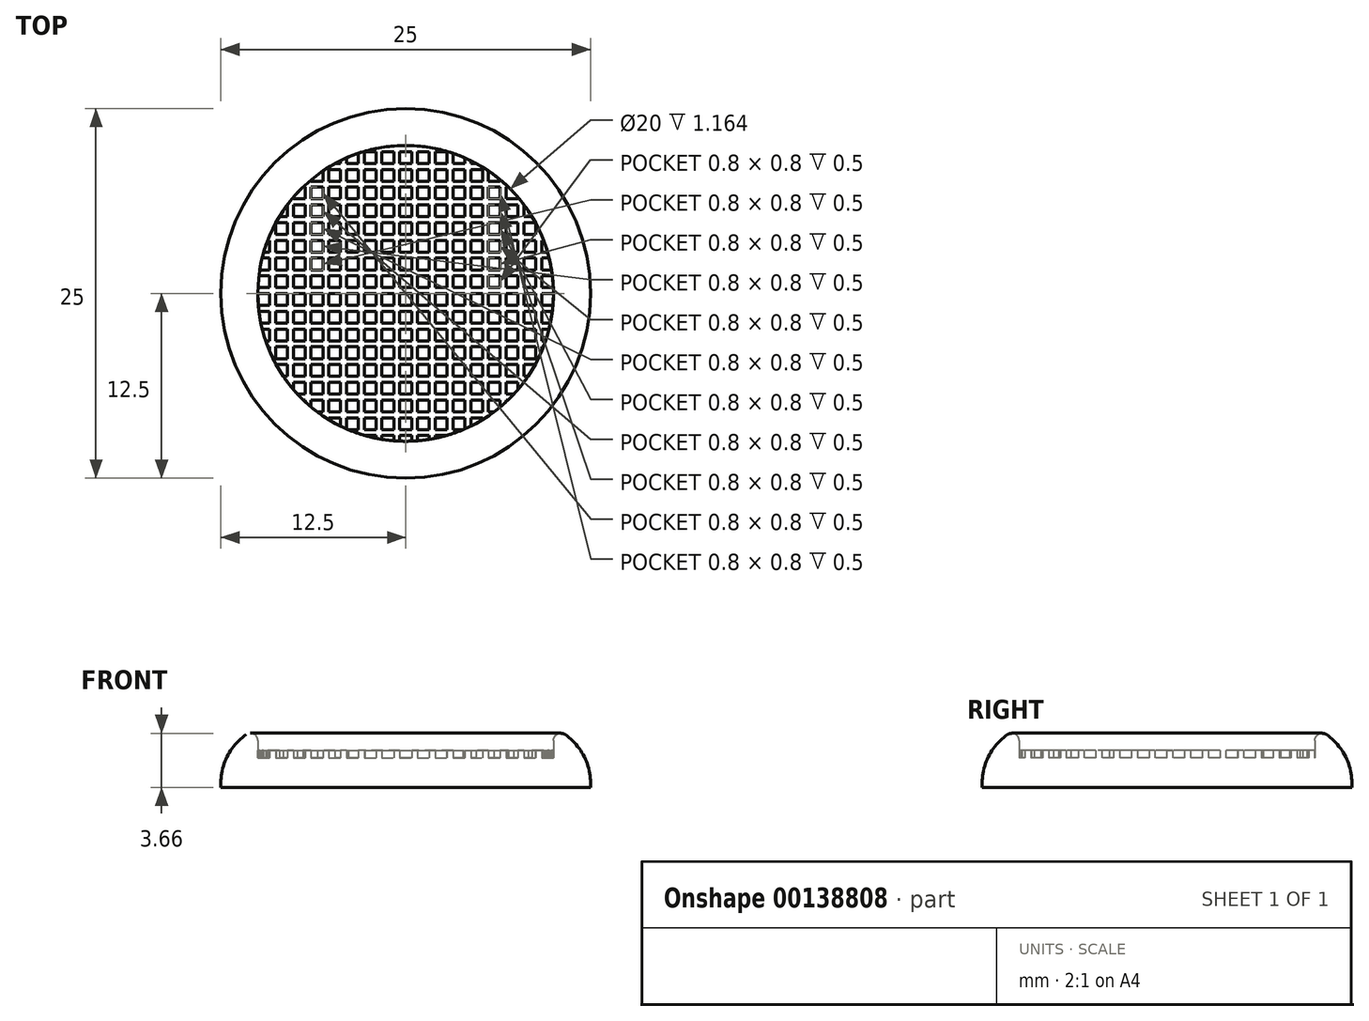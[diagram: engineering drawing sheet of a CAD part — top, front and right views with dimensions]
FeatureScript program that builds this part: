
annotation { "Feature Type Name" : "Feature", "Feature Type Description" : "" }
export const myFeature = defineFeature(function(context is Context, id is Id, definition is map)
    precondition{}
    {
        {
            var Q0;
            Q0=qCreatedBy(makeId("Top.planeOp"),FACE);
            var sketch = newSketch(context, id + "F0", { "sketchPlane" : qUnion([Q0])});
            skCircle(sketch, "E0", {"center": v(0, 0) * mm, "radius": 12.5 * mm});
            skCircle(sketch, "E1", {"center": v(0, 0) * mm, "radius": 10 * mm});
            skSolve(sketch);
        }
        {
            var Q0;
            Q0=makeQuery(id+"F0.imprint","IMPRINT",FACE,{"disambiguationData":[TD([[makeQuery(id+"F0.imprint","IMPRINT",EDGE,{"derivedFrom":sQuery(id+"F0.wireOp",EDGE,"E0")}),1.0]])]});
            var Q1;
            Q1=makeQuery(id+"F0.imprint","IMPRINT",FACE,{"disambiguationData":[TD([[makeQuery(id+"F0.imprint","IMPRINT",EDGE,{"derivedFrom":sQuery(id+"F0.wireOp",EDGE,"E1")}),1.0]])]});
            extrude(context, id + "F1", {"entities" : qUnion([Q0, Q1]), "depth" : 2 * mm});
        }
        {
            var Q0;
            Q0=makeQuery(id+"F0.imprint","IMPRINT",FACE,{"disambiguationData":[TD([[makeQuery(id+"F0.imprint","IMPRINT",EDGE,{"derivedFrom":sQuery(id+"F0.wireOp",EDGE,"E0")}),1.0]])]});
            extrude(context, id + "F2", {"entities" : qUnion([Q0]), "operationType" : NewBodyOperationType.ADD, "depth" : 4 * mm});
        }
        {
            var Q0;
            Q0=makeQuery(id+"F2.opExtrude","CAP_EDGE",EDGE,{"disambiguationData":[OSD([sQuery(id+"F0.wireOp",EDGE,"E0")])],"isStart":false});
            fillet(context, id + "F3", {"entities" : qUnion([Q0]), "radius" : 4 * mm, "tangentPropagation" : true, "allowEdgeOverflow" : false});
        }
        {
            var Q0;
            Q0=makeQuery(id+"F3.opFillet","BLEND_EDGE",EDGE,{"blendedFrom":[makeQuery(id+"F2.opExtrude","CAP_EDGE",EDGE,{"disambiguationData":[OSD([sQuery(id+"F0.wireOp",EDGE,"E0")])],"isStart":false}),makeQuery(id+"F2.opExtrude","SWEPT_FACE",FACE,{"disambiguationData":[OSD([sQuery(id+"F0.wireOp",EDGE,"E1")])]})],"blendedInto":[makeQuery(id+"F2.opExtrude","SWEPT_FACE",FACE,{"disambiguationData":[OSD([sQuery(id+"F0.wireOp",EDGE,"E1")])]})]});
            fillet(context, id + "F4", {"entities" : qUnion([Q0]), "radius" : 0.5 * mm, "tangentPropagation" : true, "allowEdgeOverflow" : false});
        }
        {
            var Q0;
            Q0=makeQuery(id+"F1.opExtrude","CAP_FACE",FACE,{"disambiguationData":[OSD([sQuery(id+"F0.wireOp",EDGE,"E0")])],"isStart":false});
            var sketch = newSketch(context, id + "F5", { "sketchPlane" : qUnion([Q0])});
            skLineSegment(sketch, "E2.bottom", {"start": v(-10, 10.79) * mm, "end": v(-9.2, 10.79) * mm});
            skLineSegment(sketch, "E2.top", {"start": v(-10, 9.99) * mm, "end": v(-9.2, 9.99) * mm});
            skLineSegment(sketch, "E2.left", {"start": v(-10, 10.79) * mm, "end": v(-10, 9.99) * mm});
            skLineSegment(sketch, "E2.right", {"start": v(-9.2, 10.79) * mm, "end": v(-9.2, 9.99) * mm});
            skCircle(sketch, "E3.0", {"center": v(0, 0) * mm, "radius": 10 * mm, "construction": true});
            skLineSegment(sketch, "E4", {"start": v(-10, 0) * mm, "end": v(-10, 10.79) * mm, "construction": true});
            skLineSegment(sketch, "E5", {"start": v(-10, 10.79) * mm, "end": v(0, 10.79) * mm, "construction": true});
            skLineSegment(sketch, "E6.1.0.0", {"start": v(-8.8, 10.79) * mm, "end": v(-8, 10.79) * mm});
            skLineSegment(sketch, "E6.1.0.1", {"start": v(-8.8, 9.99) * mm, "end": v(-8, 9.99) * mm});
            skLineSegment(sketch, "E6.1.0.2", {"start": v(-8, 10.79) * mm, "end": v(-8, 9.99) * mm});
            skLineSegment(sketch, "E6.1.0.3", {"start": v(-8.8, 10.79) * mm, "end": v(-8.8, 9.99) * mm});
            skLineSegment(sketch, "E6.2.0.0", {"start": v(-7.6, 10.79) * mm, "end": v(-6.8, 10.79) * mm});
            skLineSegment(sketch, "E6.2.0.1", {"start": v(-7.6, 9.99) * mm, "end": v(-6.8, 9.99) * mm});
            skLineSegment(sketch, "E6.2.0.2", {"start": v(-6.8, 10.79) * mm, "end": v(-6.8, 9.99) * mm});
            skLineSegment(sketch, "E6.2.0.3", {"start": v(-7.6, 10.79) * mm, "end": v(-7.6, 9.99) * mm});
            skLineSegment(sketch, "E6.3.0.0", {"start": v(-6.4, 10.79) * mm, "end": v(-5.6, 10.79) * mm});
            skLineSegment(sketch, "E6.3.0.1", {"start": v(-6.4, 9.99) * mm, "end": v(-5.6, 9.99) * mm});
            skLineSegment(sketch, "E6.3.0.2", {"start": v(-5.6, 10.79) * mm, "end": v(-5.6, 9.99) * mm});
            skLineSegment(sketch, "E6.3.0.3", {"start": v(-6.4, 10.79) * mm, "end": v(-6.4, 9.99) * mm});
            skLineSegment(sketch, "E6.4.0.0", {"start": v(-5.2, 10.79) * mm, "end": v(-4.4, 10.79) * mm});
            skLineSegment(sketch, "E6.4.0.1", {"start": v(-5.2, 9.99) * mm, "end": v(-4.4, 9.99) * mm});
            skLineSegment(sketch, "E6.4.0.2", {"start": v(-4.4, 10.79) * mm, "end": v(-4.4, 9.99) * mm});
            skLineSegment(sketch, "E6.4.0.3", {"start": v(-5.2, 10.79) * mm, "end": v(-5.2, 9.99) * mm});
            skLineSegment(sketch, "E6.5.0.0", {"start": v(-4, 10.79) * mm, "end": v(-3.2, 10.79) * mm});
            skLineSegment(sketch, "E6.5.0.1", {"start": v(-4, 9.99) * mm, "end": v(-3.2, 9.99) * mm});
            skLineSegment(sketch, "E6.5.0.2", {"start": v(-3.2, 10.79) * mm, "end": v(-3.2, 9.99) * mm});
            skLineSegment(sketch, "E6.5.0.3", {"start": v(-4, 10.79) * mm, "end": v(-4, 9.99) * mm});
            skLineSegment(sketch, "E6.6.0.0", {"start": v(-2.8, 10.79) * mm, "end": v(-2, 10.79) * mm});
            skLineSegment(sketch, "E6.6.0.1", {"start": v(-2.8, 9.99) * mm, "end": v(-2, 9.99) * mm});
            skLineSegment(sketch, "E6.6.0.2", {"start": v(-2, 10.79) * mm, "end": v(-2, 9.99) * mm});
            skLineSegment(sketch, "E6.6.0.3", {"start": v(-2.8, 10.79) * mm, "end": v(-2.8, 9.99) * mm});
            skLineSegment(sketch, "E6.7.0.0", {"start": v(-1.6, 10.79) * mm, "end": v(-0.8, 10.79) * mm});
            skLineSegment(sketch, "E6.7.0.1", {"start": v(-1.6, 9.99) * mm, "end": v(-0.8, 9.99) * mm});
            skLineSegment(sketch, "E6.7.0.2", {"start": v(-0.8, 10.79) * mm, "end": v(-0.8, 9.99) * mm});
            skLineSegment(sketch, "E6.7.0.3", {"start": v(-1.6, 10.79) * mm, "end": v(-1.6, 9.99) * mm});
            skLineSegment(sketch, "E6.8.0.0", {"start": v(-0.4, 10.79) * mm, "end": v(0.4, 10.79) * mm});
            skLineSegment(sketch, "E6.8.0.1", {"start": v(-0.4, 9.99) * mm, "end": v(0.4, 9.99) * mm});
            skLineSegment(sketch, "E6.8.0.2", {"start": v(0.4, 10.79) * mm, "end": v(0.4, 9.99) * mm});
            skLineSegment(sketch, "E6.8.0.3", {"start": v(-0.4, 10.79) * mm, "end": v(-0.4, 9.99) * mm});
            skLineSegment(sketch, "E6.9.0.0", {"start": v(0.8, 10.79) * mm, "end": v(1.6, 10.79) * mm});
            skLineSegment(sketch, "E6.9.0.1", {"start": v(0.8, 9.99) * mm, "end": v(1.6, 9.99) * mm});
            skLineSegment(sketch, "E6.9.0.2", {"start": v(1.6, 10.79) * mm, "end": v(1.6, 9.99) * mm});
            skLineSegment(sketch, "E6.9.0.3", {"start": v(0.8, 10.79) * mm, "end": v(0.8, 9.99) * mm});
            skLineSegment(sketch, "E6.10.0.0", {"start": v(2, 10.79) * mm, "end": v(2.8, 10.79) * mm});
            skLineSegment(sketch, "E6.10.0.1", {"start": v(2, 9.99) * mm, "end": v(2.8, 9.99) * mm});
            skLineSegment(sketch, "E6.10.0.2", {"start": v(2.8, 10.79) * mm, "end": v(2.8, 9.99) * mm});
            skLineSegment(sketch, "E6.10.0.3", {"start": v(2, 10.79) * mm, "end": v(2, 9.99) * mm});
            skLineSegment(sketch, "E6.11.0.0", {"start": v(3.2, 10.79) * mm, "end": v(4, 10.79) * mm});
            skLineSegment(sketch, "E6.11.0.1", {"start": v(3.2, 9.99) * mm, "end": v(4, 9.99) * mm});
            skLineSegment(sketch, "E6.11.0.2", {"start": v(4, 10.79) * mm, "end": v(4, 9.99) * mm});
            skLineSegment(sketch, "E6.11.0.3", {"start": v(3.2, 10.79) * mm, "end": v(3.2, 9.99) * mm});
            skLineSegment(sketch, "E6.12.0.0", {"start": v(4.4, 10.79) * mm, "end": v(5.2, 10.79) * mm});
            skLineSegment(sketch, "E6.12.0.1", {"start": v(4.4, 9.99) * mm, "end": v(5.2, 9.99) * mm});
            skLineSegment(sketch, "E6.12.0.2", {"start": v(5.2, 10.79) * mm, "end": v(5.2, 9.99) * mm});
            skLineSegment(sketch, "E6.12.0.3", {"start": v(4.4, 10.79) * mm, "end": v(4.4, 9.99) * mm});
            skLineSegment(sketch, "E6.13.0.0", {"start": v(5.6, 10.79) * mm, "end": v(6.4, 10.79) * mm});
            skLineSegment(sketch, "E6.13.0.1", {"start": v(5.6, 9.99) * mm, "end": v(6.4, 9.99) * mm});
            skLineSegment(sketch, "E6.13.0.2", {"start": v(6.4, 10.79) * mm, "end": v(6.4, 9.99) * mm});
            skLineSegment(sketch, "E6.13.0.3", {"start": v(5.6, 10.79) * mm, "end": v(5.6, 9.99) * mm});
            skLineSegment(sketch, "E6.14.0.0", {"start": v(6.8, 10.79) * mm, "end": v(7.6, 10.79) * mm});
            skLineSegment(sketch, "E6.14.0.1", {"start": v(6.8, 9.99) * mm, "end": v(7.6, 9.99) * mm});
            skLineSegment(sketch, "E6.14.0.2", {"start": v(7.6, 10.79) * mm, "end": v(7.6, 9.99) * mm});
            skLineSegment(sketch, "E6.14.0.3", {"start": v(6.8, 10.79) * mm, "end": v(6.8, 9.99) * mm});
            skLineSegment(sketch, "E6.15.0.0", {"start": v(8, 10.79) * mm, "end": v(8.8, 10.79) * mm});
            skLineSegment(sketch, "E6.15.0.1", {"start": v(8, 9.99) * mm, "end": v(8.8, 9.99) * mm});
            skLineSegment(sketch, "E6.15.0.2", {"start": v(8.8, 10.79) * mm, "end": v(8.8, 9.99) * mm});
            skLineSegment(sketch, "E6.15.0.3", {"start": v(8, 10.79) * mm, "end": v(8, 9.99) * mm});
            skLineSegment(sketch, "E6.16.0.0", {"start": v(9.2, 10.79) * mm, "end": v(10, 10.79) * mm});
            skLineSegment(sketch, "E6.16.0.1", {"start": v(9.2, 9.99) * mm, "end": v(10, 9.99) * mm});
            skLineSegment(sketch, "E6.16.0.2", {"start": v(10, 10.79) * mm, "end": v(10, 9.99) * mm});
            skLineSegment(sketch, "E6.16.0.3", {"start": v(9.2, 10.79) * mm, "end": v(9.2, 9.99) * mm});
            skLineSegment(sketch, "E6.direction1", {"start": v(-10, 9.99) * mm, "end": v(-8.8, 9.99) * mm, "construction": true});
            skLineSegment(sketch, "E7.1.0.0", {"start": v(6.8, 9.59) * mm, "end": v(6.8, 8.79) * mm});
            skLineSegment(sketch, "E7.1.0.1", {"start": v(6.8, 8.79) * mm, "end": v(7.6, 8.79) * mm});
            skLineSegment(sketch, "E7.1.0.2", {"start": v(6.8, 9.59) * mm, "end": v(7.6, 9.59) * mm});
            skLineSegment(sketch, "E7.1.0.3", {"start": v(6.4, 9.59) * mm, "end": v(6.4, 8.79) * mm});
            skLineSegment(sketch, "E7.1.0.4", {"start": v(5.6, 8.79) * mm, "end": v(6.4, 8.79) * mm});
            skLineSegment(sketch, "E7.1.0.5", {"start": v(5.6, 9.59) * mm, "end": v(6.4, 9.59) * mm});
            skLineSegment(sketch, "E7.1.0.6", {"start": v(10, 9.59) * mm, "end": v(10, 8.79) * mm});
            skLineSegment(sketch, "E7.1.0.7", {"start": v(9.2, 8.79) * mm, "end": v(10, 8.79) * mm});
            skLineSegment(sketch, "E7.1.0.8", {"start": v(9.2, 9.59) * mm, "end": v(10, 9.59) * mm});
            skLineSegment(sketch, "E7.1.0.9", {"start": v(2, 9.59) * mm, "end": v(2, 8.79) * mm});
            skLineSegment(sketch, "E7.1.0.10", {"start": v(-2.8, 9.59) * mm, "end": v(-2.8, 8.79) * mm});
            skLineSegment(sketch, "E7.1.0.11", {"start": v(-7.6, 8.79) * mm, "end": v(-6.8, 8.79) * mm});
            skLineSegment(sketch, "E7.1.0.12", {"start": v(-7.6, 9.59) * mm, "end": v(-6.8, 9.59) * mm});
            skLineSegment(sketch, "E7.1.0.13", {"start": v(-2.8, 8.79) * mm, "end": v(-2, 8.79) * mm});
            skLineSegment(sketch, "E7.1.0.14", {"start": v(2, 8.79) * mm, "end": v(2.8, 8.79) * mm});
            skLineSegment(sketch, "E7.1.0.15", {"start": v(-8.8, 9.59) * mm, "end": v(-8.8, 8.79) * mm});
            skLineSegment(sketch, "E7.1.0.16", {"start": v(-8, 9.59) * mm, "end": v(-8, 8.79) * mm});
            skLineSegment(sketch, "E7.1.0.17", {"start": v(-8.8, 8.79) * mm, "end": v(-8, 8.79) * mm});
            skLineSegment(sketch, "E7.1.0.18", {"start": v(-10, 9.59) * mm, "end": v(0, 9.59) * mm, "construction": true});
            skLineSegment(sketch, "E7.1.0.19", {"start": v(-9.2, 9.59) * mm, "end": v(-9.2, 8.79) * mm});
            skLineSegment(sketch, "E7.1.0.20", {"start": v(-6.4, 9.59) * mm, "end": v(-5.6, 9.59) * mm});
            skLineSegment(sketch, "E7.1.0.21", {"start": v(-7.6, 9.59) * mm, "end": v(-7.6, 8.79) * mm});
            skLineSegment(sketch, "E7.1.0.22", {"start": v(-6.8, 9.59) * mm, "end": v(-6.8, 8.79) * mm});
            skLineSegment(sketch, "E7.1.0.23", {"start": v(2.8, 9.59) * mm, "end": v(2.8, 8.79) * mm});
            skLineSegment(sketch, "E7.1.0.24", {"start": v(7.6, 9.59) * mm, "end": v(7.6, 8.79) * mm});
            skLineSegment(sketch, "E7.1.0.25", {"start": v(-2, 9.59) * mm, "end": v(-2, 8.79) * mm});
            skLineSegment(sketch, "E7.1.0.26", {"start": v(2, 9.59) * mm, "end": v(2.8, 9.59) * mm});
            skLineSegment(sketch, "E7.1.0.27", {"start": v(-4, 9.59) * mm, "end": v(-4, 8.79) * mm});
            skLineSegment(sketch, "E7.1.0.28", {"start": v(0.8, 9.59) * mm, "end": v(0.8, 8.79) * mm});
            skLineSegment(sketch, "E7.1.0.29", {"start": v(5.6, 9.59) * mm, "end": v(5.6, 8.79) * mm});
            skLineSegment(sketch, "E7.1.0.30", {"start": v(-3.2, 9.59) * mm, "end": v(-3.2, 8.79) * mm});
            skLineSegment(sketch, "E7.1.0.31", {"start": v(1.6, 9.59) * mm, "end": v(1.6, 8.79) * mm});
            skLineSegment(sketch, "E7.1.0.32", {"start": v(-4, 8.79) * mm, "end": v(-3.2, 8.79) * mm});
            skLineSegment(sketch, "E7.1.0.33", {"start": v(0.8, 8.79) * mm, "end": v(1.6, 8.79) * mm});
            skLineSegment(sketch, "E7.1.0.34", {"start": v(0.8, 9.59) * mm, "end": v(1.6, 9.59) * mm});
            skLineSegment(sketch, "E7.1.0.35", {"start": v(-10, 8.79) * mm, "end": v(-8.8, 8.79) * mm, "construction": true});
            skLineSegment(sketch, "E7.1.0.36", {"start": v(4.4, 9.59) * mm, "end": v(4.4, 8.79) * mm});
            skLineSegment(sketch, "E7.1.0.37", {"start": v(9.2, 9.59) * mm, "end": v(9.2, 8.79) * mm});
            skLineSegment(sketch, "E7.1.0.38", {"start": v(-5.2, 9.59) * mm, "end": v(-5.2, 8.79) * mm});
            skLineSegment(sketch, "E7.1.0.39", {"start": v(-0.4, 9.59) * mm, "end": v(-0.4, 8.79) * mm});
            skLineSegment(sketch, "E7.1.0.40", {"start": v(5.2, 9.59) * mm, "end": v(5.2, 8.79) * mm});
            skLineSegment(sketch, "E7.1.0.41", {"start": v(-4.4, 9.59) * mm, "end": v(-4.4, 8.79) * mm});
            skLineSegment(sketch, "E7.1.0.42", {"start": v(0.4, 9.59) * mm, "end": v(0.4, 8.79) * mm});
            skLineSegment(sketch, "E7.1.0.43", {"start": v(4.4, 8.79) * mm, "end": v(5.2, 8.79) * mm});
            skLineSegment(sketch, "E7.1.0.44", {"start": v(-5.2, 8.79) * mm, "end": v(-4.4, 8.79) * mm});
            skLineSegment(sketch, "E7.1.0.45", {"start": v(-0.4, 8.79) * mm, "end": v(0.4, 8.79) * mm});
            skLineSegment(sketch, "E7.1.0.46", {"start": v(4.4, 9.59) * mm, "end": v(5.2, 9.59) * mm});
            skLineSegment(sketch, "E7.1.0.47", {"start": v(-0.4, 9.59) * mm, "end": v(0.4, 9.59) * mm});
            skLineSegment(sketch, "E7.1.0.48", {"start": v(3.2, 9.59) * mm, "end": v(3.2, 8.79) * mm});
            skLineSegment(sketch, "E7.1.0.49", {"start": v(8, 9.59) * mm, "end": v(8, 8.79) * mm});
            skLineSegment(sketch, "E7.1.0.50", {"start": v(-6.4, 9.59) * mm, "end": v(-6.4, 8.79) * mm});
            skLineSegment(sketch, "E7.1.0.51", {"start": v(-1.6, 9.59) * mm, "end": v(-1.6, 8.79) * mm});
            skLineSegment(sketch, "E7.1.0.52", {"start": v(-5.6, 9.59) * mm, "end": v(-5.6, 8.79) * mm});
            skLineSegment(sketch, "E7.1.0.53", {"start": v(-0.8, 9.59) * mm, "end": v(-0.8, 8.79) * mm});
            skLineSegment(sketch, "E7.1.0.54", {"start": v(4, 9.59) * mm, "end": v(4, 8.79) * mm});
            skLineSegment(sketch, "E7.1.0.55", {"start": v(8.8, 9.59) * mm, "end": v(8.8, 8.79) * mm});
            skLineSegment(sketch, "E7.1.0.56", {"start": v(3.2, 8.79) * mm, "end": v(4, 8.79) * mm});
            skLineSegment(sketch, "E7.1.0.57", {"start": v(8, 8.79) * mm, "end": v(8.8, 8.79) * mm});
            skLineSegment(sketch, "E7.1.0.58", {"start": v(-6.4, 8.79) * mm, "end": v(-5.6, 8.79) * mm});
            skLineSegment(sketch, "E7.1.0.59", {"start": v(-1.6, 8.79) * mm, "end": v(-0.8, 8.79) * mm});
            skLineSegment(sketch, "E7.1.0.60", {"start": v(3.2, 9.59) * mm, "end": v(4, 9.59) * mm});
            skLineSegment(sketch, "E7.1.0.61", {"start": v(8, 9.59) * mm, "end": v(8.8, 9.59) * mm});
            skLineSegment(sketch, "E7.1.0.62", {"start": v(-8.8, 9.59) * mm, "end": v(-8, 9.59) * mm});
            skLineSegment(sketch, "E7.1.0.63", {"start": v(-10, 9.59) * mm, "end": v(-10, 8.79) * mm});
            skLineSegment(sketch, "E7.1.0.64", {"start": v(-10, 8.79) * mm, "end": v(-9.2, 8.79) * mm});
            skLineSegment(sketch, "E7.1.0.65", {"start": v(-10, 9.59) * mm, "end": v(-9.2, 9.59) * mm});
            skLineSegment(sketch, "E7.1.0.66", {"start": v(-2.8, 9.59) * mm, "end": v(-2, 9.59) * mm});
            skLineSegment(sketch, "E7.1.0.67", {"start": v(-4, 9.59) * mm, "end": v(-3.2, 9.59) * mm});
            skLineSegment(sketch, "E7.1.0.68", {"start": v(-5.2, 9.59) * mm, "end": v(-4.4, 9.59) * mm});
            skLineSegment(sketch, "E7.1.0.69", {"start": v(-1.6, 9.59) * mm, "end": v(-0.8, 9.59) * mm});
            skLineSegment(sketch, "E7.2.0.0", {"start": v(6.8, 8.39) * mm, "end": v(6.8, 7.59) * mm});
            skLineSegment(sketch, "E7.2.0.1", {"start": v(6.8, 7.59) * mm, "end": v(7.6, 7.59) * mm});
            skLineSegment(sketch, "E7.2.0.2", {"start": v(6.8, 8.39) * mm, "end": v(7.6, 8.39) * mm});
            skLineSegment(sketch, "E7.2.0.3", {"start": v(6.4, 8.39) * mm, "end": v(6.4, 7.59) * mm});
            skLineSegment(sketch, "E7.2.0.4", {"start": v(5.6, 7.59) * mm, "end": v(6.4, 7.59) * mm});
            skLineSegment(sketch, "E7.2.0.5", {"start": v(5.6, 8.39) * mm, "end": v(6.4, 8.39) * mm});
            skLineSegment(sketch, "E7.2.0.6", {"start": v(10, 8.39) * mm, "end": v(10, 7.59) * mm});
            skLineSegment(sketch, "E7.2.0.7", {"start": v(9.2, 7.59) * mm, "end": v(10, 7.59) * mm});
            skLineSegment(sketch, "E7.2.0.8", {"start": v(9.2, 8.39) * mm, "end": v(10, 8.39) * mm});
            skLineSegment(sketch, "E7.2.0.9", {"start": v(2, 8.39) * mm, "end": v(2, 7.59) * mm});
            skLineSegment(sketch, "E7.2.0.10", {"start": v(-2.8, 8.39) * mm, "end": v(-2.8, 7.59) * mm});
            skLineSegment(sketch, "E7.2.0.11", {"start": v(-7.6, 7.59) * mm, "end": v(-6.8, 7.59) * mm});
            skLineSegment(sketch, "E7.2.0.12", {"start": v(-7.6, 8.39) * mm, "end": v(-6.8, 8.39) * mm});
            skLineSegment(sketch, "E7.2.0.13", {"start": v(-2.8, 7.59) * mm, "end": v(-2, 7.59) * mm});
            skLineSegment(sketch, "E7.2.0.14", {"start": v(2, 7.59) * mm, "end": v(2.8, 7.59) * mm});
            skLineSegment(sketch, "E7.2.0.15", {"start": v(-8.8, 8.39) * mm, "end": v(-8.8, 7.59) * mm});
            skLineSegment(sketch, "E7.2.0.16", {"start": v(-8, 8.39) * mm, "end": v(-8, 7.59) * mm});
            skLineSegment(sketch, "E7.2.0.17", {"start": v(-8.8, 7.59) * mm, "end": v(-8, 7.59) * mm});
            skLineSegment(sketch, "E7.2.0.18", {"start": v(-10, 8.39) * mm, "end": v(0, 8.39) * mm, "construction": true});
            skLineSegment(sketch, "E7.2.0.19", {"start": v(-9.2, 8.39) * mm, "end": v(-9.2, 7.59) * mm});
            skLineSegment(sketch, "E7.2.0.20", {"start": v(-6.4, 8.39) * mm, "end": v(-5.6, 8.39) * mm});
            skLineSegment(sketch, "E7.2.0.21", {"start": v(-7.6, 8.39) * mm, "end": v(-7.6, 7.59) * mm});
            skLineSegment(sketch, "E7.2.0.22", {"start": v(-6.8, 8.39) * mm, "end": v(-6.8, 7.59) * mm});
            skLineSegment(sketch, "E7.2.0.23", {"start": v(2.8, 8.39) * mm, "end": v(2.8, 7.59) * mm});
            skLineSegment(sketch, "E7.2.0.24", {"start": v(7.6, 8.39) * mm, "end": v(7.6, 7.59) * mm});
            skLineSegment(sketch, "E7.2.0.25", {"start": v(-2, 8.39) * mm, "end": v(-2, 7.59) * mm});
            skLineSegment(sketch, "E7.2.0.26", {"start": v(2, 8.39) * mm, "end": v(2.8, 8.39) * mm});
            skLineSegment(sketch, "E7.2.0.27", {"start": v(-4, 8.39) * mm, "end": v(-4, 7.59) * mm});
            skLineSegment(sketch, "E7.2.0.28", {"start": v(0.8, 8.39) * mm, "end": v(0.8, 7.59) * mm});
            skLineSegment(sketch, "E7.2.0.29", {"start": v(5.6, 8.39) * mm, "end": v(5.6, 7.59) * mm});
            skLineSegment(sketch, "E7.2.0.30", {"start": v(-3.2, 8.39) * mm, "end": v(-3.2, 7.59) * mm});
            skLineSegment(sketch, "E7.2.0.31", {"start": v(1.6, 8.39) * mm, "end": v(1.6, 7.59) * mm});
            skLineSegment(sketch, "E7.2.0.32", {"start": v(-4, 7.59) * mm, "end": v(-3.2, 7.59) * mm});
            skLineSegment(sketch, "E7.2.0.33", {"start": v(0.8, 7.59) * mm, "end": v(1.6, 7.59) * mm});
            skLineSegment(sketch, "E7.2.0.34", {"start": v(0.8, 8.39) * mm, "end": v(1.6, 8.39) * mm});
            skLineSegment(sketch, "E7.2.0.35", {"start": v(-10, 7.59) * mm, "end": v(-8.8, 7.59) * mm, "construction": true});
            skLineSegment(sketch, "E7.2.0.36", {"start": v(4.4, 8.39) * mm, "end": v(4.4, 7.59) * mm});
            skLineSegment(sketch, "E7.2.0.37", {"start": v(9.2, 8.39) * mm, "end": v(9.2, 7.59) * mm});
            skLineSegment(sketch, "E7.2.0.38", {"start": v(-5.2, 8.39) * mm, "end": v(-5.2, 7.59) * mm});
            skLineSegment(sketch, "E7.2.0.39", {"start": v(-0.4, 8.39) * mm, "end": v(-0.4, 7.59) * mm});
            skLineSegment(sketch, "E7.2.0.40", {"start": v(5.2, 8.39) * mm, "end": v(5.2, 7.59) * mm});
            skLineSegment(sketch, "E7.2.0.41", {"start": v(-4.4, 8.39) * mm, "end": v(-4.4, 7.59) * mm});
            skLineSegment(sketch, "E7.2.0.42", {"start": v(0.4, 8.39) * mm, "end": v(0.4, 7.59) * mm});
            skLineSegment(sketch, "E7.2.0.43", {"start": v(4.4, 7.59) * mm, "end": v(5.2, 7.59) * mm});
            skLineSegment(sketch, "E7.2.0.44", {"start": v(-5.2, 7.59) * mm, "end": v(-4.4, 7.59) * mm});
            skLineSegment(sketch, "E7.2.0.45", {"start": v(-0.4, 7.59) * mm, "end": v(0.4, 7.59) * mm});
            skLineSegment(sketch, "E7.2.0.46", {"start": v(4.4, 8.39) * mm, "end": v(5.2, 8.39) * mm});
            skLineSegment(sketch, "E7.2.0.47", {"start": v(-0.4, 8.39) * mm, "end": v(0.4, 8.39) * mm});
            skLineSegment(sketch, "E7.2.0.48", {"start": v(3.2, 8.39) * mm, "end": v(3.2, 7.59) * mm});
            skLineSegment(sketch, "E7.2.0.49", {"start": v(8, 8.39) * mm, "end": v(8, 7.59) * mm});
            skLineSegment(sketch, "E7.2.0.50", {"start": v(-6.4, 8.39) * mm, "end": v(-6.4, 7.59) * mm});
            skLineSegment(sketch, "E7.2.0.51", {"start": v(-1.6, 8.39) * mm, "end": v(-1.6, 7.59) * mm});
            skLineSegment(sketch, "E7.2.0.52", {"start": v(-5.6, 8.39) * mm, "end": v(-5.6, 7.59) * mm});
            skLineSegment(sketch, "E7.2.0.53", {"start": v(-0.8, 8.39) * mm, "end": v(-0.8, 7.59) * mm});
            skLineSegment(sketch, "E7.2.0.54", {"start": v(4, 8.39) * mm, "end": v(4, 7.59) * mm});
            skLineSegment(sketch, "E7.2.0.55", {"start": v(8.8, 8.39) * mm, "end": v(8.8, 7.59) * mm});
            skLineSegment(sketch, "E7.2.0.56", {"start": v(3.2, 7.59) * mm, "end": v(4, 7.59) * mm});
            skLineSegment(sketch, "E7.2.0.57", {"start": v(8, 7.59) * mm, "end": v(8.8, 7.59) * mm});
            skLineSegment(sketch, "E7.2.0.58", {"start": v(-6.4, 7.59) * mm, "end": v(-5.6, 7.59) * mm});
            skLineSegment(sketch, "E7.2.0.59", {"start": v(-1.6, 7.59) * mm, "end": v(-0.8, 7.59) * mm});
            skLineSegment(sketch, "E7.2.0.60", {"start": v(3.2, 8.39) * mm, "end": v(4, 8.39) * mm});
            skLineSegment(sketch, "E7.2.0.61", {"start": v(8, 8.39) * mm, "end": v(8.8, 8.39) * mm});
            skLineSegment(sketch, "E7.2.0.62", {"start": v(-8.8, 8.39) * mm, "end": v(-8, 8.39) * mm});
            skLineSegment(sketch, "E7.2.0.63", {"start": v(-10, 8.39) * mm, "end": v(-10, 7.59) * mm});
            skLineSegment(sketch, "E7.2.0.64", {"start": v(-10, 7.59) * mm, "end": v(-9.2, 7.59) * mm});
            skLineSegment(sketch, "E7.2.0.65", {"start": v(-10, 8.39) * mm, "end": v(-9.2, 8.39) * mm});
            skLineSegment(sketch, "E7.2.0.66", {"start": v(-2.8, 8.39) * mm, "end": v(-2, 8.39) * mm});
            skLineSegment(sketch, "E7.2.0.67", {"start": v(-4, 8.39) * mm, "end": v(-3.2, 8.39) * mm});
            skLineSegment(sketch, "E7.2.0.68", {"start": v(-5.2, 8.39) * mm, "end": v(-4.4, 8.39) * mm});
            skLineSegment(sketch, "E7.2.0.69", {"start": v(-1.6, 8.39) * mm, "end": v(-0.8, 8.39) * mm});
            skLineSegment(sketch, "E7.direction1", {"start": v(-10, 9.99) * mm, "end": v(-10, 8.79) * mm, "construction": true});
            skLineSegment(sketch, "E8.0.3.0", {"start": v(6.8, 7.19) * mm, "end": v(6.8, 6.39) * mm});
            skLineSegment(sketch, "E8.3.3.0", {"start": v(6.8, 6.39) * mm, "end": v(7.6, 6.39) * mm});
            skLineSegment(sketch, "E8.6.3.0", {"start": v(6.8, 7.19) * mm, "end": v(7.6, 7.19) * mm});
            skLineSegment(sketch, "E8.9.3.0", {"start": v(6.4, 7.19) * mm, "end": v(6.4, 6.39) * mm});
            skLineSegment(sketch, "E8.12.3.0", {"start": v(5.6, 6.39) * mm, "end": v(6.4, 6.39) * mm});
            skLineSegment(sketch, "E8.15.3.0", {"start": v(5.6, 7.19) * mm, "end": v(6.4, 7.19) * mm});
            skLineSegment(sketch, "E8.18.3.0", {"start": v(10, 7.19) * mm, "end": v(10, 6.39) * mm});
            skLineSegment(sketch, "E8.21.3.0", {"start": v(9.2, 6.39) * mm, "end": v(10, 6.39) * mm});
            skLineSegment(sketch, "E8.24.3.0", {"start": v(9.2, 7.19) * mm, "end": v(10, 7.19) * mm});
            skLineSegment(sketch, "E8.27.3.0", {"start": v(2, 7.19) * mm, "end": v(2, 6.39) * mm});
            skLineSegment(sketch, "E8.30.3.0", {"start": v(-2.8, 7.19) * mm, "end": v(-2.8, 6.39) * mm});
            skLineSegment(sketch, "E8.33.3.0", {"start": v(-7.6, 6.39) * mm, "end": v(-6.8, 6.39) * mm});
            skLineSegment(sketch, "E8.36.3.0", {"start": v(-7.6, 7.19) * mm, "end": v(-6.8, 7.19) * mm});
            skLineSegment(sketch, "E8.39.3.0", {"start": v(-2.8, 6.39) * mm, "end": v(-2, 6.39) * mm});
            skLineSegment(sketch, "E8.42.3.0", {"start": v(2, 6.39) * mm, "end": v(2.8, 6.39) * mm});
            skLineSegment(sketch, "E8.45.3.0", {"start": v(-8.8, 7.19) * mm, "end": v(-8.8, 6.39) * mm});
            skLineSegment(sketch, "E8.48.3.0", {"start": v(-8, 7.19) * mm, "end": v(-8, 6.39) * mm});
            skLineSegment(sketch, "E8.51.3.0", {"start": v(-8.8, 6.39) * mm, "end": v(-8, 6.39) * mm});
            skLineSegment(sketch, "E8.54.3.0", {"start": v(-10, 7.19) * mm, "end": v(0, 7.19) * mm, "construction": true});
            skLineSegment(sketch, "E8.57.3.0", {"start": v(-9.2, 7.19) * mm, "end": v(-9.2, 6.39) * mm});
            skLineSegment(sketch, "E8.60.3.0", {"start": v(-6.4, 7.19) * mm, "end": v(-5.6, 7.19) * mm});
            skLineSegment(sketch, "E8.63.3.0", {"start": v(-7.6, 7.19) * mm, "end": v(-7.6, 6.39) * mm});
            skLineSegment(sketch, "E8.66.3.0", {"start": v(-6.8, 7.19) * mm, "end": v(-6.8, 6.39) * mm});
            skLineSegment(sketch, "E8.69.3.0", {"start": v(2.8, 7.19) * mm, "end": v(2.8, 6.39) * mm});
            skLineSegment(sketch, "E8.72.3.0", {"start": v(7.6, 7.19) * mm, "end": v(7.6, 6.39) * mm});
            skLineSegment(sketch, "E8.75.3.0", {"start": v(-2, 7.19) * mm, "end": v(-2, 6.39) * mm});
            skLineSegment(sketch, "E8.78.3.0", {"start": v(2, 7.19) * mm, "end": v(2.8, 7.19) * mm});
            skLineSegment(sketch, "E8.81.3.0", {"start": v(-4, 7.19) * mm, "end": v(-4, 6.39) * mm});
            skLineSegment(sketch, "E8.84.3.0", {"start": v(0.8, 7.19) * mm, "end": v(0.8, 6.39) * mm});
            skLineSegment(sketch, "E8.87.3.0", {"start": v(5.6, 7.19) * mm, "end": v(5.6, 6.39) * mm});
            skLineSegment(sketch, "E8.90.3.0", {"start": v(-3.2, 7.19) * mm, "end": v(-3.2, 6.39) * mm});
            skLineSegment(sketch, "E8.93.3.0", {"start": v(1.6, 7.19) * mm, "end": v(1.6, 6.39) * mm});
            skLineSegment(sketch, "E8.96.3.0", {"start": v(-4, 6.39) * mm, "end": v(-3.2, 6.39) * mm});
            skLineSegment(sketch, "E8.99.3.0", {"start": v(0.8, 6.39) * mm, "end": v(1.6, 6.39) * mm});
            skLineSegment(sketch, "E8.102.3.0", {"start": v(0.8, 7.19) * mm, "end": v(1.6, 7.19) * mm});
            skLineSegment(sketch, "E8.105.3.0", {"start": v(-10, 6.39) * mm, "end": v(-8.8, 6.39) * mm, "construction": true});
            skLineSegment(sketch, "E8.108.3.0", {"start": v(4.4, 7.19) * mm, "end": v(4.4, 6.39) * mm});
            skLineSegment(sketch, "E8.111.3.0", {"start": v(9.2, 7.19) * mm, "end": v(9.2, 6.39) * mm});
            skLineSegment(sketch, "E8.114.3.0", {"start": v(-5.2, 7.19) * mm, "end": v(-5.2, 6.39) * mm});
            skLineSegment(sketch, "E8.117.3.0", {"start": v(-0.4, 7.19) * mm, "end": v(-0.4, 6.39) * mm});
            skLineSegment(sketch, "E8.120.3.0", {"start": v(5.2, 7.19) * mm, "end": v(5.2, 6.39) * mm});
            skLineSegment(sketch, "E8.123.3.0", {"start": v(-4.4, 7.19) * mm, "end": v(-4.4, 6.39) * mm});
            skLineSegment(sketch, "E8.126.3.0", {"start": v(0.4, 7.19) * mm, "end": v(0.4, 6.39) * mm});
            skLineSegment(sketch, "E8.129.3.0", {"start": v(4.4, 6.39) * mm, "end": v(5.2, 6.39) * mm});
            skLineSegment(sketch, "E8.132.3.0", {"start": v(-5.2, 6.39) * mm, "end": v(-4.4, 6.39) * mm});
            skLineSegment(sketch, "E8.135.3.0", {"start": v(-0.4, 6.39) * mm, "end": v(0.4, 6.39) * mm});
            skLineSegment(sketch, "E8.138.3.0", {"start": v(4.4, 7.19) * mm, "end": v(5.2, 7.19) * mm});
            skLineSegment(sketch, "E8.141.3.0", {"start": v(-0.4, 7.19) * mm, "end": v(0.4, 7.19) * mm});
            skLineSegment(sketch, "E8.144.3.0", {"start": v(3.2, 7.19) * mm, "end": v(3.2, 6.39) * mm});
            skLineSegment(sketch, "E8.147.3.0", {"start": v(8, 7.19) * mm, "end": v(8, 6.39) * mm});
            skLineSegment(sketch, "E8.150.3.0", {"start": v(-6.4, 7.19) * mm, "end": v(-6.4, 6.39) * mm});
            skLineSegment(sketch, "E8.153.3.0", {"start": v(-1.6, 7.19) * mm, "end": v(-1.6, 6.39) * mm});
            skLineSegment(sketch, "E8.156.3.0", {"start": v(-5.6, 7.19) * mm, "end": v(-5.6, 6.39) * mm});
            skLineSegment(sketch, "E8.159.3.0", {"start": v(-0.8, 7.19) * mm, "end": v(-0.8, 6.39) * mm});
            skLineSegment(sketch, "E8.162.3.0", {"start": v(4, 7.19) * mm, "end": v(4, 6.39) * mm});
            skLineSegment(sketch, "E8.165.3.0", {"start": v(8.8, 7.19) * mm, "end": v(8.8, 6.39) * mm});
            skLineSegment(sketch, "E8.168.3.0", {"start": v(3.2, 6.39) * mm, "end": v(4, 6.39) * mm});
            skLineSegment(sketch, "E8.171.3.0", {"start": v(8, 6.39) * mm, "end": v(8.8, 6.39) * mm});
            skLineSegment(sketch, "E8.174.3.0", {"start": v(-6.4, 6.39) * mm, "end": v(-5.6, 6.39) * mm});
            skLineSegment(sketch, "E8.177.3.0", {"start": v(-1.6, 6.39) * mm, "end": v(-0.8, 6.39) * mm});
            skLineSegment(sketch, "E8.180.3.0", {"start": v(3.2, 7.19) * mm, "end": v(4, 7.19) * mm});
            skLineSegment(sketch, "E8.183.3.0", {"start": v(8, 7.19) * mm, "end": v(8.8, 7.19) * mm});
            skLineSegment(sketch, "E8.186.3.0", {"start": v(-8.8, 7.19) * mm, "end": v(-8, 7.19) * mm});
            skLineSegment(sketch, "E8.189.3.0", {"start": v(-10, 7.19) * mm, "end": v(-10, 6.39) * mm});
            skLineSegment(sketch, "E8.192.3.0", {"start": v(-10, 6.39) * mm, "end": v(-9.2, 6.39) * mm});
            skLineSegment(sketch, "E8.195.3.0", {"start": v(-10, 7.19) * mm, "end": v(-9.2, 7.19) * mm});
            skLineSegment(sketch, "E8.198.3.0", {"start": v(-2.8, 7.19) * mm, "end": v(-2, 7.19) * mm});
            skLineSegment(sketch, "E8.201.3.0", {"start": v(-4, 7.19) * mm, "end": v(-3.2, 7.19) * mm});
            skLineSegment(sketch, "E8.204.3.0", {"start": v(-5.2, 7.19) * mm, "end": v(-4.4, 7.19) * mm});
            skLineSegment(sketch, "E8.207.3.0", {"start": v(-1.6, 7.19) * mm, "end": v(-0.8, 7.19) * mm});
            skLineSegment(sketch, "E8.0.4.0", {"start": v(6.8, 5.99) * mm, "end": v(6.8, 5.19) * mm});
            skLineSegment(sketch, "E8.3.4.0", {"start": v(6.8, 5.19) * mm, "end": v(7.6, 5.19) * mm});
            skLineSegment(sketch, "E8.6.4.0", {"start": v(6.8, 5.99) * mm, "end": v(7.6, 5.99) * mm});
            skLineSegment(sketch, "E8.9.4.0", {"start": v(6.4, 5.99) * mm, "end": v(6.4, 5.19) * mm});
            skLineSegment(sketch, "E8.12.4.0", {"start": v(5.6, 5.19) * mm, "end": v(6.4, 5.19) * mm});
            skLineSegment(sketch, "E8.15.4.0", {"start": v(5.6, 5.99) * mm, "end": v(6.4, 5.99) * mm});
            skLineSegment(sketch, "E8.18.4.0", {"start": v(10, 5.99) * mm, "end": v(10, 5.19) * mm});
            skLineSegment(sketch, "E8.21.4.0", {"start": v(9.2, 5.19) * mm, "end": v(10, 5.19) * mm});
            skLineSegment(sketch, "E8.24.4.0", {"start": v(9.2, 5.99) * mm, "end": v(10, 5.99) * mm});
            skLineSegment(sketch, "E8.27.4.0", {"start": v(2, 5.99) * mm, "end": v(2, 5.19) * mm});
            skLineSegment(sketch, "E8.30.4.0", {"start": v(-2.8, 5.99) * mm, "end": v(-2.8, 5.19) * mm});
            skLineSegment(sketch, "E8.33.4.0", {"start": v(-7.6, 5.19) * mm, "end": v(-6.8, 5.19) * mm});
            skLineSegment(sketch, "E8.36.4.0", {"start": v(-7.6, 5.99) * mm, "end": v(-6.8, 5.99) * mm});
            skLineSegment(sketch, "E8.39.4.0", {"start": v(-2.8, 5.19) * mm, "end": v(-2, 5.19) * mm});
            skLineSegment(sketch, "E8.42.4.0", {"start": v(2, 5.19) * mm, "end": v(2.8, 5.19) * mm});
            skLineSegment(sketch, "E8.45.4.0", {"start": v(-8.8, 5.99) * mm, "end": v(-8.8, 5.19) * mm});
            skLineSegment(sketch, "E8.48.4.0", {"start": v(-8, 5.99) * mm, "end": v(-8, 5.19) * mm});
            skLineSegment(sketch, "E8.51.4.0", {"start": v(-8.8, 5.19) * mm, "end": v(-8, 5.19) * mm});
            skLineSegment(sketch, "E8.54.4.0", {"start": v(-10, 5.99) * mm, "end": v(0, 5.99) * mm, "construction": true});
            skLineSegment(sketch, "E8.57.4.0", {"start": v(-9.2, 5.99) * mm, "end": v(-9.2, 5.19) * mm});
            skLineSegment(sketch, "E8.60.4.0", {"start": v(-6.4, 5.99) * mm, "end": v(-5.6, 5.99) * mm});
            skLineSegment(sketch, "E8.63.4.0", {"start": v(-7.6, 5.99) * mm, "end": v(-7.6, 5.19) * mm});
            skLineSegment(sketch, "E8.66.4.0", {"start": v(-6.8, 5.99) * mm, "end": v(-6.8, 5.19) * mm});
            skLineSegment(sketch, "E8.69.4.0", {"start": v(2.8, 5.99) * mm, "end": v(2.8, 5.19) * mm});
            skLineSegment(sketch, "E8.72.4.0", {"start": v(7.6, 5.99) * mm, "end": v(7.6, 5.19) * mm});
            skLineSegment(sketch, "E8.75.4.0", {"start": v(-2, 5.99) * mm, "end": v(-2, 5.19) * mm});
            skLineSegment(sketch, "E8.78.4.0", {"start": v(2, 5.99) * mm, "end": v(2.8, 5.99) * mm});
            skLineSegment(sketch, "E8.81.4.0", {"start": v(-4, 5.99) * mm, "end": v(-4, 5.19) * mm});
            skLineSegment(sketch, "E8.84.4.0", {"start": v(0.8, 5.99) * mm, "end": v(0.8, 5.19) * mm});
            skLineSegment(sketch, "E8.87.4.0", {"start": v(5.6, 5.99) * mm, "end": v(5.6, 5.19) * mm});
            skLineSegment(sketch, "E8.90.4.0", {"start": v(-3.2, 5.99) * mm, "end": v(-3.2, 5.19) * mm});
            skLineSegment(sketch, "E8.93.4.0", {"start": v(1.6, 5.99) * mm, "end": v(1.6, 5.19) * mm});
            skLineSegment(sketch, "E8.96.4.0", {"start": v(-4, 5.19) * mm, "end": v(-3.2, 5.19) * mm});
            skLineSegment(sketch, "E8.99.4.0", {"start": v(0.8, 5.19) * mm, "end": v(1.6, 5.19) * mm});
            skLineSegment(sketch, "E8.102.4.0", {"start": v(0.8, 5.99) * mm, "end": v(1.6, 5.99) * mm});
            skLineSegment(sketch, "E8.105.4.0", {"start": v(-10, 5.19) * mm, "end": v(-8.8, 5.19) * mm, "construction": true});
            skLineSegment(sketch, "E8.108.4.0", {"start": v(4.4, 5.99) * mm, "end": v(4.4, 5.19) * mm});
            skLineSegment(sketch, "E8.111.4.0", {"start": v(9.2, 5.99) * mm, "end": v(9.2, 5.19) * mm});
            skLineSegment(sketch, "E8.114.4.0", {"start": v(-5.2, 5.99) * mm, "end": v(-5.2, 5.19) * mm});
            skLineSegment(sketch, "E8.117.4.0", {"start": v(-0.4, 5.99) * mm, "end": v(-0.4, 5.19) * mm});
            skLineSegment(sketch, "E8.120.4.0", {"start": v(5.2, 5.99) * mm, "end": v(5.2, 5.19) * mm});
            skLineSegment(sketch, "E8.123.4.0", {"start": v(-4.4, 5.99) * mm, "end": v(-4.4, 5.19) * mm});
            skLineSegment(sketch, "E8.126.4.0", {"start": v(0.4, 5.99) * mm, "end": v(0.4, 5.19) * mm});
            skLineSegment(sketch, "E8.129.4.0", {"start": v(4.4, 5.19) * mm, "end": v(5.2, 5.19) * mm});
            skLineSegment(sketch, "E8.132.4.0", {"start": v(-5.2, 5.19) * mm, "end": v(-4.4, 5.19) * mm});
            skLineSegment(sketch, "E8.135.4.0", {"start": v(-0.4, 5.19) * mm, "end": v(0.4, 5.19) * mm});
            skLineSegment(sketch, "E8.138.4.0", {"start": v(4.4, 5.99) * mm, "end": v(5.2, 5.99) * mm});
            skLineSegment(sketch, "E8.141.4.0", {"start": v(-0.4, 5.99) * mm, "end": v(0.4, 5.99) * mm});
            skLineSegment(sketch, "E8.144.4.0", {"start": v(3.2, 5.99) * mm, "end": v(3.2, 5.19) * mm});
            skLineSegment(sketch, "E8.147.4.0", {"start": v(8, 5.99) * mm, "end": v(8, 5.19) * mm});
            skLineSegment(sketch, "E8.150.4.0", {"start": v(-6.4, 5.99) * mm, "end": v(-6.4, 5.19) * mm});
            skLineSegment(sketch, "E8.153.4.0", {"start": v(-1.6, 5.99) * mm, "end": v(-1.6, 5.19) * mm});
            skLineSegment(sketch, "E8.156.4.0", {"start": v(-5.6, 5.99) * mm, "end": v(-5.6, 5.19) * mm});
            skLineSegment(sketch, "E8.159.4.0", {"start": v(-0.8, 5.99) * mm, "end": v(-0.8, 5.19) * mm});
            skLineSegment(sketch, "E8.162.4.0", {"start": v(4, 5.99) * mm, "end": v(4, 5.19) * mm});
            skLineSegment(sketch, "E8.165.4.0", {"start": v(8.8, 5.99) * mm, "end": v(8.8, 5.19) * mm});
            skLineSegment(sketch, "E8.168.4.0", {"start": v(3.2, 5.19) * mm, "end": v(4, 5.19) * mm});
            skLineSegment(sketch, "E8.171.4.0", {"start": v(8, 5.19) * mm, "end": v(8.8, 5.19) * mm});
            skLineSegment(sketch, "E8.174.4.0", {"start": v(-6.4, 5.19) * mm, "end": v(-5.6, 5.19) * mm});
            skLineSegment(sketch, "E8.177.4.0", {"start": v(-1.6, 5.19) * mm, "end": v(-0.8, 5.19) * mm});
            skLineSegment(sketch, "E8.180.4.0", {"start": v(3.2, 5.99) * mm, "end": v(4, 5.99) * mm});
            skLineSegment(sketch, "E8.183.4.0", {"start": v(8, 5.99) * mm, "end": v(8.8, 5.99) * mm});
            skLineSegment(sketch, "E8.186.4.0", {"start": v(-8.8, 5.99) * mm, "end": v(-8, 5.99) * mm});
            skLineSegment(sketch, "E8.189.4.0", {"start": v(-10, 5.99) * mm, "end": v(-10, 5.19) * mm});
            skLineSegment(sketch, "E8.192.4.0", {"start": v(-10, 5.19) * mm, "end": v(-9.2, 5.19) * mm});
            skLineSegment(sketch, "E8.195.4.0", {"start": v(-10, 5.99) * mm, "end": v(-9.2, 5.99) * mm});
            skLineSegment(sketch, "E8.198.4.0", {"start": v(-2.8, 5.99) * mm, "end": v(-2, 5.99) * mm});
            skLineSegment(sketch, "E8.201.4.0", {"start": v(-4, 5.99) * mm, "end": v(-3.2, 5.99) * mm});
            skLineSegment(sketch, "E8.204.4.0", {"start": v(-5.2, 5.99) * mm, "end": v(-4.4, 5.99) * mm});
            skLineSegment(sketch, "E8.207.4.0", {"start": v(-1.6, 5.99) * mm, "end": v(-0.8, 5.99) * mm});
            skLineSegment(sketch, "E8.0.5.0", {"start": v(6.8, 4.79) * mm, "end": v(6.8, 3.99) * mm});
            skLineSegment(sketch, "E8.3.5.0", {"start": v(6.8, 3.99) * mm, "end": v(7.6, 3.99) * mm});
            skLineSegment(sketch, "E8.6.5.0", {"start": v(6.8, 4.79) * mm, "end": v(7.6, 4.79) * mm});
            skLineSegment(sketch, "E8.9.5.0", {"start": v(6.4, 4.79) * mm, "end": v(6.4, 3.99) * mm});
            skLineSegment(sketch, "E8.12.5.0", {"start": v(5.6, 3.99) * mm, "end": v(6.4, 3.99) * mm});
            skLineSegment(sketch, "E8.15.5.0", {"start": v(5.6, 4.79) * mm, "end": v(6.4, 4.79) * mm});
            skLineSegment(sketch, "E8.18.5.0", {"start": v(10, 4.79) * mm, "end": v(10, 3.99) * mm});
            skLineSegment(sketch, "E8.21.5.0", {"start": v(9.2, 3.99) * mm, "end": v(10, 3.99) * mm});
            skLineSegment(sketch, "E8.24.5.0", {"start": v(9.2, 4.79) * mm, "end": v(10, 4.79) * mm});
            skLineSegment(sketch, "E8.27.5.0", {"start": v(2, 4.79) * mm, "end": v(2, 3.99) * mm});
            skLineSegment(sketch, "E8.30.5.0", {"start": v(-2.8, 4.79) * mm, "end": v(-2.8, 3.99) * mm});
            skLineSegment(sketch, "E8.33.5.0", {"start": v(-7.6, 3.99) * mm, "end": v(-6.8, 3.99) * mm});
            skLineSegment(sketch, "E8.36.5.0", {"start": v(-7.6, 4.79) * mm, "end": v(-6.8, 4.79) * mm});
            skLineSegment(sketch, "E8.39.5.0", {"start": v(-2.8, 3.99) * mm, "end": v(-2, 3.99) * mm});
            skLineSegment(sketch, "E8.42.5.0", {"start": v(2, 3.99) * mm, "end": v(2.8, 3.99) * mm});
            skLineSegment(sketch, "E8.45.5.0", {"start": v(-8.8, 4.79) * mm, "end": v(-8.8, 3.99) * mm});
            skLineSegment(sketch, "E8.48.5.0", {"start": v(-8, 4.79) * mm, "end": v(-8, 3.99) * mm});
            skLineSegment(sketch, "E8.51.5.0", {"start": v(-8.8, 3.99) * mm, "end": v(-8, 3.99) * mm});
            skLineSegment(sketch, "E8.54.5.0", {"start": v(-10, 4.79) * mm, "end": v(0, 4.79) * mm, "construction": true});
            skLineSegment(sketch, "E8.57.5.0", {"start": v(-9.2, 4.79) * mm, "end": v(-9.2, 3.99) * mm});
            skLineSegment(sketch, "E8.60.5.0", {"start": v(-6.4, 4.79) * mm, "end": v(-5.6, 4.79) * mm});
            skLineSegment(sketch, "E8.63.5.0", {"start": v(-7.6, 4.79) * mm, "end": v(-7.6, 3.99) * mm});
            skLineSegment(sketch, "E8.66.5.0", {"start": v(-6.8, 4.79) * mm, "end": v(-6.8, 3.99) * mm});
            skLineSegment(sketch, "E8.69.5.0", {"start": v(2.8, 4.79) * mm, "end": v(2.8, 3.99) * mm});
            skLineSegment(sketch, "E8.72.5.0", {"start": v(7.6, 4.79) * mm, "end": v(7.6, 3.99) * mm});
            skLineSegment(sketch, "E8.75.5.0", {"start": v(-2, 4.79) * mm, "end": v(-2, 3.99) * mm});
            skLineSegment(sketch, "E8.78.5.0", {"start": v(2, 4.79) * mm, "end": v(2.8, 4.79) * mm});
            skLineSegment(sketch, "E8.81.5.0", {"start": v(-4, 4.79) * mm, "end": v(-4, 3.99) * mm});
            skLineSegment(sketch, "E8.84.5.0", {"start": v(0.8, 4.79) * mm, "end": v(0.8, 3.99) * mm});
            skLineSegment(sketch, "E8.87.5.0", {"start": v(5.6, 4.79) * mm, "end": v(5.6, 3.99) * mm});
            skLineSegment(sketch, "E8.90.5.0", {"start": v(-3.2, 4.79) * mm, "end": v(-3.2, 3.99) * mm});
            skLineSegment(sketch, "E8.93.5.0", {"start": v(1.6, 4.79) * mm, "end": v(1.6, 3.99) * mm});
            skLineSegment(sketch, "E8.96.5.0", {"start": v(-4, 3.99) * mm, "end": v(-3.2, 3.99) * mm});
            skLineSegment(sketch, "E8.99.5.0", {"start": v(0.8, 3.99) * mm, "end": v(1.6, 3.99) * mm});
            skLineSegment(sketch, "E8.102.5.0", {"start": v(0.8, 4.79) * mm, "end": v(1.6, 4.79) * mm});
            skLineSegment(sketch, "E8.105.5.0", {"start": v(-10, 3.99) * mm, "end": v(-8.8, 3.99) * mm, "construction": true});
            skLineSegment(sketch, "E8.108.5.0", {"start": v(4.4, 4.79) * mm, "end": v(4.4, 3.99) * mm});
            skLineSegment(sketch, "E8.111.5.0", {"start": v(9.2, 4.79) * mm, "end": v(9.2, 3.99) * mm});
            skLineSegment(sketch, "E8.114.5.0", {"start": v(-5.2, 4.79) * mm, "end": v(-5.2, 3.99) * mm});
            skLineSegment(sketch, "E8.117.5.0", {"start": v(-0.4, 4.79) * mm, "end": v(-0.4, 3.99) * mm});
            skLineSegment(sketch, "E8.120.5.0", {"start": v(5.2, 4.79) * mm, "end": v(5.2, 3.99) * mm});
            skLineSegment(sketch, "E8.123.5.0", {"start": v(-4.4, 4.79) * mm, "end": v(-4.4, 3.99) * mm});
            skLineSegment(sketch, "E8.126.5.0", {"start": v(0.4, 4.79) * mm, "end": v(0.4, 3.99) * mm});
            skLineSegment(sketch, "E8.129.5.0", {"start": v(4.4, 3.99) * mm, "end": v(5.2, 3.99) * mm});
            skLineSegment(sketch, "E8.132.5.0", {"start": v(-5.2, 3.99) * mm, "end": v(-4.4, 3.99) * mm});
            skLineSegment(sketch, "E8.135.5.0", {"start": v(-0.4, 3.99) * mm, "end": v(0.4, 3.99) * mm});
            skLineSegment(sketch, "E8.138.5.0", {"start": v(4.4, 4.79) * mm, "end": v(5.2, 4.79) * mm});
            skLineSegment(sketch, "E8.141.5.0", {"start": v(-0.4, 4.79) * mm, "end": v(0.4, 4.79) * mm});
            skLineSegment(sketch, "E8.144.5.0", {"start": v(3.2, 4.79) * mm, "end": v(3.2, 3.99) * mm});
            skLineSegment(sketch, "E8.147.5.0", {"start": v(8, 4.79) * mm, "end": v(8, 3.99) * mm});
            skLineSegment(sketch, "E8.150.5.0", {"start": v(-6.4, 4.79) * mm, "end": v(-6.4, 3.99) * mm});
            skLineSegment(sketch, "E8.153.5.0", {"start": v(-1.6, 4.79) * mm, "end": v(-1.6, 3.99) * mm});
            skLineSegment(sketch, "E8.156.5.0", {"start": v(-5.6, 4.79) * mm, "end": v(-5.6, 3.99) * mm});
            skLineSegment(sketch, "E8.159.5.0", {"start": v(-0.8, 4.79) * mm, "end": v(-0.8, 3.99) * mm});
            skLineSegment(sketch, "E8.162.5.0", {"start": v(4, 4.79) * mm, "end": v(4, 3.99) * mm});
            skLineSegment(sketch, "E8.165.5.0", {"start": v(8.8, 4.79) * mm, "end": v(8.8, 3.99) * mm});
            skLineSegment(sketch, "E8.168.5.0", {"start": v(3.2, 3.99) * mm, "end": v(4, 3.99) * mm});
            skLineSegment(sketch, "E8.171.5.0", {"start": v(8, 3.99) * mm, "end": v(8.8, 3.99) * mm});
            skLineSegment(sketch, "E8.174.5.0", {"start": v(-6.4, 3.99) * mm, "end": v(-5.6, 3.99) * mm});
            skLineSegment(sketch, "E8.177.5.0", {"start": v(-1.6, 3.99) * mm, "end": v(-0.8, 3.99) * mm});
            skLineSegment(sketch, "E8.180.5.0", {"start": v(3.2, 4.79) * mm, "end": v(4, 4.79) * mm});
            skLineSegment(sketch, "E8.183.5.0", {"start": v(8, 4.79) * mm, "end": v(8.8, 4.79) * mm});
            skLineSegment(sketch, "E8.186.5.0", {"start": v(-8.8, 4.79) * mm, "end": v(-8, 4.79) * mm});
            skLineSegment(sketch, "E8.189.5.0", {"start": v(-10, 4.79) * mm, "end": v(-10, 3.99) * mm});
            skLineSegment(sketch, "E8.192.5.0", {"start": v(-10, 3.99) * mm, "end": v(-9.2, 3.99) * mm});
            skLineSegment(sketch, "E8.195.5.0", {"start": v(-10, 4.79) * mm, "end": v(-9.2, 4.79) * mm});
            skLineSegment(sketch, "E8.198.5.0", {"start": v(-2.8, 4.79) * mm, "end": v(-2, 4.79) * mm});
            skLineSegment(sketch, "E8.201.5.0", {"start": v(-4, 4.79) * mm, "end": v(-3.2, 4.79) * mm});
            skLineSegment(sketch, "E8.204.5.0", {"start": v(-5.2, 4.79) * mm, "end": v(-4.4, 4.79) * mm});
            skLineSegment(sketch, "E8.207.5.0", {"start": v(-1.6, 4.79) * mm, "end": v(-0.8, 4.79) * mm});
            skLineSegment(sketch, "E8.0.6.0", {"start": v(6.8, 3.59) * mm, "end": v(6.8, 2.79) * mm});
            skLineSegment(sketch, "E8.3.6.0", {"start": v(6.8, 2.79) * mm, "end": v(7.6, 2.79) * mm});
            skLineSegment(sketch, "E8.6.6.0", {"start": v(6.8, 3.59) * mm, "end": v(7.6, 3.59) * mm});
            skLineSegment(sketch, "E8.9.6.0", {"start": v(6.4, 3.59) * mm, "end": v(6.4, 2.79) * mm});
            skLineSegment(sketch, "E8.12.6.0", {"start": v(5.6, 2.79) * mm, "end": v(6.4, 2.79) * mm});
            skLineSegment(sketch, "E8.15.6.0", {"start": v(5.6, 3.59) * mm, "end": v(6.4, 3.59) * mm});
            skLineSegment(sketch, "E8.18.6.0", {"start": v(10, 3.59) * mm, "end": v(10, 2.79) * mm});
            skLineSegment(sketch, "E8.21.6.0", {"start": v(9.2, 2.79) * mm, "end": v(10, 2.79) * mm});
            skLineSegment(sketch, "E8.24.6.0", {"start": v(9.2, 3.59) * mm, "end": v(10, 3.59) * mm});
            skLineSegment(sketch, "E8.27.6.0", {"start": v(2, 3.59) * mm, "end": v(2, 2.79) * mm});
            skLineSegment(sketch, "E8.30.6.0", {"start": v(-2.8, 3.59) * mm, "end": v(-2.8, 2.79) * mm});
            skLineSegment(sketch, "E8.33.6.0", {"start": v(-7.6, 2.79) * mm, "end": v(-6.8, 2.79) * mm});
            skLineSegment(sketch, "E8.36.6.0", {"start": v(-7.6, 3.59) * mm, "end": v(-6.8, 3.59) * mm});
            skLineSegment(sketch, "E8.39.6.0", {"start": v(-2.8, 2.79) * mm, "end": v(-2, 2.79) * mm});
            skLineSegment(sketch, "E8.42.6.0", {"start": v(2, 2.79) * mm, "end": v(2.8, 2.79) * mm});
            skLineSegment(sketch, "E8.45.6.0", {"start": v(-8.8, 3.59) * mm, "end": v(-8.8, 2.79) * mm});
            skLineSegment(sketch, "E8.48.6.0", {"start": v(-8, 3.59) * mm, "end": v(-8, 2.79) * mm});
            skLineSegment(sketch, "E8.51.6.0", {"start": v(-8.8, 2.79) * mm, "end": v(-8, 2.79) * mm});
            skLineSegment(sketch, "E8.54.6.0", {"start": v(-10, 3.59) * mm, "end": v(0, 3.59) * mm, "construction": true});
            skLineSegment(sketch, "E8.57.6.0", {"start": v(-9.2, 3.59) * mm, "end": v(-9.2, 2.79) * mm});
            skLineSegment(sketch, "E8.60.6.0", {"start": v(-6.4, 3.59) * mm, "end": v(-5.6, 3.59) * mm});
            skLineSegment(sketch, "E8.63.6.0", {"start": v(-7.6, 3.59) * mm, "end": v(-7.6, 2.79) * mm});
            skLineSegment(sketch, "E8.66.6.0", {"start": v(-6.8, 3.59) * mm, "end": v(-6.8, 2.79) * mm});
            skLineSegment(sketch, "E8.69.6.0", {"start": v(2.8, 3.59) * mm, "end": v(2.8, 2.79) * mm});
            skLineSegment(sketch, "E8.72.6.0", {"start": v(7.6, 3.59) * mm, "end": v(7.6, 2.79) * mm});
            skLineSegment(sketch, "E8.75.6.0", {"start": v(-2, 3.59) * mm, "end": v(-2, 2.79) * mm});
            skLineSegment(sketch, "E8.78.6.0", {"start": v(2, 3.59) * mm, "end": v(2.8, 3.59) * mm});
            skLineSegment(sketch, "E8.81.6.0", {"start": v(-4, 3.59) * mm, "end": v(-4, 2.79) * mm});
            skLineSegment(sketch, "E8.84.6.0", {"start": v(0.8, 3.59) * mm, "end": v(0.8, 2.79) * mm});
            skLineSegment(sketch, "E8.87.6.0", {"start": v(5.6, 3.59) * mm, "end": v(5.6, 2.79) * mm});
            skLineSegment(sketch, "E8.90.6.0", {"start": v(-3.2, 3.59) * mm, "end": v(-3.2, 2.79) * mm});
            skLineSegment(sketch, "E8.93.6.0", {"start": v(1.6, 3.59) * mm, "end": v(1.6, 2.79) * mm});
            skLineSegment(sketch, "E8.96.6.0", {"start": v(-4, 2.79) * mm, "end": v(-3.2, 2.79) * mm});
            skLineSegment(sketch, "E8.99.6.0", {"start": v(0.8, 2.79) * mm, "end": v(1.6, 2.79) * mm});
            skLineSegment(sketch, "E8.102.6.0", {"start": v(0.8, 3.59) * mm, "end": v(1.6, 3.59) * mm});
            skLineSegment(sketch, "E8.105.6.0", {"start": v(-10, 2.79) * mm, "end": v(-8.8, 2.79) * mm, "construction": true});
            skLineSegment(sketch, "E8.108.6.0", {"start": v(4.4, 3.59) * mm, "end": v(4.4, 2.79) * mm});
            skLineSegment(sketch, "E8.111.6.0", {"start": v(9.2, 3.59) * mm, "end": v(9.2, 2.79) * mm});
            skLineSegment(sketch, "E8.114.6.0", {"start": v(-5.2, 3.59) * mm, "end": v(-5.2, 2.79) * mm});
            skLineSegment(sketch, "E8.117.6.0", {"start": v(-0.4, 3.59) * mm, "end": v(-0.4, 2.79) * mm});
            skLineSegment(sketch, "E8.120.6.0", {"start": v(5.2, 3.59) * mm, "end": v(5.2, 2.79) * mm});
            skLineSegment(sketch, "E8.123.6.0", {"start": v(-4.4, 3.59) * mm, "end": v(-4.4, 2.79) * mm});
            skLineSegment(sketch, "E8.126.6.0", {"start": v(0.4, 3.59) * mm, "end": v(0.4, 2.79) * mm});
            skLineSegment(sketch, "E8.129.6.0", {"start": v(4.4, 2.79) * mm, "end": v(5.2, 2.79) * mm});
            skLineSegment(sketch, "E8.132.6.0", {"start": v(-5.2, 2.79) * mm, "end": v(-4.4, 2.79) * mm});
            skLineSegment(sketch, "E8.135.6.0", {"start": v(-0.4, 2.79) * mm, "end": v(0.4, 2.79) * mm});
            skLineSegment(sketch, "E8.138.6.0", {"start": v(4.4, 3.59) * mm, "end": v(5.2, 3.59) * mm});
            skLineSegment(sketch, "E8.141.6.0", {"start": v(-0.4, 3.59) * mm, "end": v(0.4, 3.59) * mm});
            skLineSegment(sketch, "E8.144.6.0", {"start": v(3.2, 3.59) * mm, "end": v(3.2, 2.79) * mm});
            skLineSegment(sketch, "E8.147.6.0", {"start": v(8, 3.59) * mm, "end": v(8, 2.79) * mm});
            skLineSegment(sketch, "E8.150.6.0", {"start": v(-6.4, 3.59) * mm, "end": v(-6.4, 2.79) * mm});
            skLineSegment(sketch, "E8.153.6.0", {"start": v(-1.6, 3.59) * mm, "end": v(-1.6, 2.79) * mm});
            skLineSegment(sketch, "E8.156.6.0", {"start": v(-5.6, 3.59) * mm, "end": v(-5.6, 2.79) * mm});
            skLineSegment(sketch, "E8.159.6.0", {"start": v(-0.8, 3.59) * mm, "end": v(-0.8, 2.79) * mm});
            skLineSegment(sketch, "E8.162.6.0", {"start": v(4, 3.59) * mm, "end": v(4, 2.79) * mm});
            skLineSegment(sketch, "E8.165.6.0", {"start": v(8.8, 3.59) * mm, "end": v(8.8, 2.79) * mm});
            skLineSegment(sketch, "E8.168.6.0", {"start": v(3.2, 2.79) * mm, "end": v(4, 2.79) * mm});
            skLineSegment(sketch, "E8.171.6.0", {"start": v(8, 2.79) * mm, "end": v(8.8, 2.79) * mm});
            skLineSegment(sketch, "E8.174.6.0", {"start": v(-6.4, 2.79) * mm, "end": v(-5.6, 2.79) * mm});
            skLineSegment(sketch, "E8.177.6.0", {"start": v(-1.6, 2.79) * mm, "end": v(-0.8, 2.79) * mm});
            skLineSegment(sketch, "E8.180.6.0", {"start": v(3.2, 3.59) * mm, "end": v(4, 3.59) * mm});
            skLineSegment(sketch, "E8.183.6.0", {"start": v(8, 3.59) * mm, "end": v(8.8, 3.59) * mm});
            skLineSegment(sketch, "E8.186.6.0", {"start": v(-8.8, 3.59) * mm, "end": v(-8, 3.59) * mm});
            skLineSegment(sketch, "E8.189.6.0", {"start": v(-10, 3.59) * mm, "end": v(-10, 2.79) * mm});
            skLineSegment(sketch, "E8.192.6.0", {"start": v(-10, 2.79) * mm, "end": v(-9.2, 2.79) * mm});
            skLineSegment(sketch, "E8.195.6.0", {"start": v(-10, 3.59) * mm, "end": v(-9.2, 3.59) * mm});
            skLineSegment(sketch, "E8.198.6.0", {"start": v(-2.8, 3.59) * mm, "end": v(-2, 3.59) * mm});
            skLineSegment(sketch, "E8.201.6.0", {"start": v(-4, 3.59) * mm, "end": v(-3.2, 3.59) * mm});
            skLineSegment(sketch, "E8.204.6.0", {"start": v(-5.2, 3.59) * mm, "end": v(-4.4, 3.59) * mm});
            skLineSegment(sketch, "E8.207.6.0", {"start": v(-1.6, 3.59) * mm, "end": v(-0.8, 3.59) * mm});
            skLineSegment(sketch, "E8.0.7.0", {"start": v(6.8, 2.39) * mm, "end": v(6.8, 1.59) * mm});
            skLineSegment(sketch, "E8.3.7.0", {"start": v(6.8, 1.59) * mm, "end": v(7.6, 1.59) * mm});
            skLineSegment(sketch, "E8.6.7.0", {"start": v(6.8, 2.39) * mm, "end": v(7.6, 2.39) * mm});
            skLineSegment(sketch, "E8.9.7.0", {"start": v(6.4, 2.39) * mm, "end": v(6.4, 1.59) * mm});
            skLineSegment(sketch, "E8.12.7.0", {"start": v(5.6, 1.59) * mm, "end": v(6.4, 1.59) * mm});
            skLineSegment(sketch, "E8.15.7.0", {"start": v(5.6, 2.39) * mm, "end": v(6.4, 2.39) * mm});
            skLineSegment(sketch, "E8.18.7.0", {"start": v(10, 2.39) * mm, "end": v(10, 1.59) * mm});
            skLineSegment(sketch, "E8.21.7.0", {"start": v(9.2, 1.59) * mm, "end": v(10, 1.59) * mm});
            skLineSegment(sketch, "E8.24.7.0", {"start": v(9.2, 2.39) * mm, "end": v(10, 2.39) * mm});
            skLineSegment(sketch, "E8.27.7.0", {"start": v(2, 2.39) * mm, "end": v(2, 1.59) * mm});
            skLineSegment(sketch, "E8.30.7.0", {"start": v(-2.8, 2.39) * mm, "end": v(-2.8, 1.59) * mm});
            skLineSegment(sketch, "E8.33.7.0", {"start": v(-7.6, 1.59) * mm, "end": v(-6.8, 1.59) * mm});
            skLineSegment(sketch, "E8.36.7.0", {"start": v(-7.6, 2.39) * mm, "end": v(-6.8, 2.39) * mm});
            skLineSegment(sketch, "E8.39.7.0", {"start": v(-2.8, 1.59) * mm, "end": v(-2, 1.59) * mm});
            skLineSegment(sketch, "E8.42.7.0", {"start": v(2, 1.59) * mm, "end": v(2.8, 1.59) * mm});
            skLineSegment(sketch, "E8.45.7.0", {"start": v(-8.8, 2.39) * mm, "end": v(-8.8, 1.59) * mm});
            skLineSegment(sketch, "E8.48.7.0", {"start": v(-8, 2.39) * mm, "end": v(-8, 1.59) * mm});
            skLineSegment(sketch, "E8.51.7.0", {"start": v(-8.8, 1.59) * mm, "end": v(-8, 1.59) * mm});
            skLineSegment(sketch, "E8.54.7.0", {"start": v(-10, 2.39) * mm, "end": v(0, 2.39) * mm, "construction": true});
            skLineSegment(sketch, "E8.57.7.0", {"start": v(-9.2, 2.39) * mm, "end": v(-9.2, 1.59) * mm});
            skLineSegment(sketch, "E8.60.7.0", {"start": v(-6.4, 2.39) * mm, "end": v(-5.6, 2.39) * mm});
            skLineSegment(sketch, "E8.63.7.0", {"start": v(-7.6, 2.39) * mm, "end": v(-7.6, 1.59) * mm});
            skLineSegment(sketch, "E8.66.7.0", {"start": v(-6.8, 2.39) * mm, "end": v(-6.8, 1.59) * mm});
            skLineSegment(sketch, "E8.69.7.0", {"start": v(2.8, 2.39) * mm, "end": v(2.8, 1.59) * mm});
            skLineSegment(sketch, "E8.72.7.0", {"start": v(7.6, 2.39) * mm, "end": v(7.6, 1.59) * mm});
            skLineSegment(sketch, "E8.75.7.0", {"start": v(-2, 2.39) * mm, "end": v(-2, 1.59) * mm});
            skLineSegment(sketch, "E8.78.7.0", {"start": v(2, 2.39) * mm, "end": v(2.8, 2.39) * mm});
            skLineSegment(sketch, "E8.81.7.0", {"start": v(-4, 2.39) * mm, "end": v(-4, 1.59) * mm});
            skLineSegment(sketch, "E8.84.7.0", {"start": v(0.8, 2.39) * mm, "end": v(0.8, 1.59) * mm});
            skLineSegment(sketch, "E8.87.7.0", {"start": v(5.6, 2.39) * mm, "end": v(5.6, 1.59) * mm});
            skLineSegment(sketch, "E8.90.7.0", {"start": v(-3.2, 2.39) * mm, "end": v(-3.2, 1.59) * mm});
            skLineSegment(sketch, "E8.93.7.0", {"start": v(1.6, 2.39) * mm, "end": v(1.6, 1.59) * mm});
            skLineSegment(sketch, "E8.96.7.0", {"start": v(-4, 1.59) * mm, "end": v(-3.2, 1.59) * mm});
            skLineSegment(sketch, "E8.99.7.0", {"start": v(0.8, 1.59) * mm, "end": v(1.6, 1.59) * mm});
            skLineSegment(sketch, "E8.102.7.0", {"start": v(0.8, 2.39) * mm, "end": v(1.6, 2.39) * mm});
            skLineSegment(sketch, "E8.105.7.0", {"start": v(-10, 1.59) * mm, "end": v(-8.8, 1.59) * mm, "construction": true});
            skLineSegment(sketch, "E8.108.7.0", {"start": v(4.4, 2.39) * mm, "end": v(4.4, 1.59) * mm});
            skLineSegment(sketch, "E8.111.7.0", {"start": v(9.2, 2.39) * mm, "end": v(9.2, 1.59) * mm});
            skLineSegment(sketch, "E8.114.7.0", {"start": v(-5.2, 2.39) * mm, "end": v(-5.2, 1.59) * mm});
            skLineSegment(sketch, "E8.117.7.0", {"start": v(-0.4, 2.39) * mm, "end": v(-0.4, 1.59) * mm});
            skLineSegment(sketch, "E8.120.7.0", {"start": v(5.2, 2.39) * mm, "end": v(5.2, 1.59) * mm});
            skLineSegment(sketch, "E8.123.7.0", {"start": v(-4.4, 2.39) * mm, "end": v(-4.4, 1.59) * mm});
            skLineSegment(sketch, "E8.126.7.0", {"start": v(0.4, 2.39) * mm, "end": v(0.4, 1.59) * mm});
            skLineSegment(sketch, "E8.129.7.0", {"start": v(4.4, 1.59) * mm, "end": v(5.2, 1.59) * mm});
            skLineSegment(sketch, "E8.132.7.0", {"start": v(-5.2, 1.59) * mm, "end": v(-4.4, 1.59) * mm});
            skLineSegment(sketch, "E8.135.7.0", {"start": v(-0.4, 1.59) * mm, "end": v(0.4, 1.59) * mm});
            skLineSegment(sketch, "E8.138.7.0", {"start": v(4.4, 2.39) * mm, "end": v(5.2, 2.39) * mm});
            skLineSegment(sketch, "E8.141.7.0", {"start": v(-0.4, 2.39) * mm, "end": v(0.4, 2.39) * mm});
            skLineSegment(sketch, "E8.144.7.0", {"start": v(3.2, 2.39) * mm, "end": v(3.2, 1.59) * mm});
            skLineSegment(sketch, "E8.147.7.0", {"start": v(8, 2.39) * mm, "end": v(8, 1.59) * mm});
            skLineSegment(sketch, "E8.150.7.0", {"start": v(-6.4, 2.39) * mm, "end": v(-6.4, 1.59) * mm});
            skLineSegment(sketch, "E8.153.7.0", {"start": v(-1.6, 2.39) * mm, "end": v(-1.6, 1.59) * mm});
            skLineSegment(sketch, "E8.156.7.0", {"start": v(-5.6, 2.39) * mm, "end": v(-5.6, 1.59) * mm});
            skLineSegment(sketch, "E8.159.7.0", {"start": v(-0.8, 2.39) * mm, "end": v(-0.8, 1.59) * mm});
            skLineSegment(sketch, "E8.162.7.0", {"start": v(4, 2.39) * mm, "end": v(4, 1.59) * mm});
            skLineSegment(sketch, "E8.165.7.0", {"start": v(8.8, 2.39) * mm, "end": v(8.8, 1.59) * mm});
            skLineSegment(sketch, "E8.168.7.0", {"start": v(3.2, 1.59) * mm, "end": v(4, 1.59) * mm});
            skLineSegment(sketch, "E8.171.7.0", {"start": v(8, 1.59) * mm, "end": v(8.8, 1.59) * mm});
            skLineSegment(sketch, "E8.174.7.0", {"start": v(-6.4, 1.59) * mm, "end": v(-5.6, 1.59) * mm});
            skLineSegment(sketch, "E8.177.7.0", {"start": v(-1.6, 1.59) * mm, "end": v(-0.8, 1.59) * mm});
            skLineSegment(sketch, "E8.180.7.0", {"start": v(3.2, 2.39) * mm, "end": v(4, 2.39) * mm});
            skLineSegment(sketch, "E8.183.7.0", {"start": v(8, 2.39) * mm, "end": v(8.8, 2.39) * mm});
            skLineSegment(sketch, "E8.186.7.0", {"start": v(-8.8, 2.39) * mm, "end": v(-8, 2.39) * mm});
            skLineSegment(sketch, "E8.189.7.0", {"start": v(-10, 2.39) * mm, "end": v(-10, 1.59) * mm});
            skLineSegment(sketch, "E8.192.7.0", {"start": v(-10, 1.59) * mm, "end": v(-9.2, 1.59) * mm});
            skLineSegment(sketch, "E8.195.7.0", {"start": v(-10, 2.39) * mm, "end": v(-9.2, 2.39) * mm});
            skLineSegment(sketch, "E8.198.7.0", {"start": v(-2.8, 2.39) * mm, "end": v(-2, 2.39) * mm});
            skLineSegment(sketch, "E8.201.7.0", {"start": v(-4, 2.39) * mm, "end": v(-3.2, 2.39) * mm});
            skLineSegment(sketch, "E8.204.7.0", {"start": v(-5.2, 2.39) * mm, "end": v(-4.4, 2.39) * mm});
            skLineSegment(sketch, "E8.207.7.0", {"start": v(-1.6, 2.39) * mm, "end": v(-0.8, 2.39) * mm});
            skLineSegment(sketch, "E8.0.8.0", {"start": v(6.8, 1.19) * mm, "end": v(6.8, 0.39) * mm});
            skLineSegment(sketch, "E8.3.8.0", {"start": v(6.8, 0.39) * mm, "end": v(7.6, 0.39) * mm});
            skLineSegment(sketch, "E8.6.8.0", {"start": v(6.8, 1.19) * mm, "end": v(7.6, 1.19) * mm});
            skLineSegment(sketch, "E8.9.8.0", {"start": v(6.4, 1.19) * mm, "end": v(6.4, 0.39) * mm});
            skLineSegment(sketch, "E8.12.8.0", {"start": v(5.6, 0.39) * mm, "end": v(6.4, 0.39) * mm});
            skLineSegment(sketch, "E8.15.8.0", {"start": v(5.6, 1.19) * mm, "end": v(6.4, 1.19) * mm});
            skLineSegment(sketch, "E8.18.8.0", {"start": v(10, 1.19) * mm, "end": v(10, 0.39) * mm});
            skLineSegment(sketch, "E8.21.8.0", {"start": v(9.2, 0.39) * mm, "end": v(10, 0.39) * mm});
            skLineSegment(sketch, "E8.24.8.0", {"start": v(9.2, 1.19) * mm, "end": v(10, 1.19) * mm});
            skLineSegment(sketch, "E8.27.8.0", {"start": v(2, 1.19) * mm, "end": v(2, 0.39) * mm});
            skLineSegment(sketch, "E8.30.8.0", {"start": v(-2.8, 1.19) * mm, "end": v(-2.8, 0.39) * mm});
            skLineSegment(sketch, "E8.33.8.0", {"start": v(-7.6, 0.39) * mm, "end": v(-6.8, 0.39) * mm});
            skLineSegment(sketch, "E8.36.8.0", {"start": v(-7.6, 1.19) * mm, "end": v(-6.8, 1.19) * mm});
            skLineSegment(sketch, "E8.39.8.0", {"start": v(-2.8, 0.39) * mm, "end": v(-2, 0.39) * mm});
            skLineSegment(sketch, "E8.42.8.0", {"start": v(2, 0.39) * mm, "end": v(2.8, 0.39) * mm});
            skLineSegment(sketch, "E8.45.8.0", {"start": v(-8.8, 1.19) * mm, "end": v(-8.8, 0.39) * mm});
            skLineSegment(sketch, "E8.48.8.0", {"start": v(-8, 1.19) * mm, "end": v(-8, 0.39) * mm});
            skLineSegment(sketch, "E8.51.8.0", {"start": v(-8.8, 0.39) * mm, "end": v(-8, 0.39) * mm});
            skLineSegment(sketch, "E8.54.8.0", {"start": v(-10, 1.19) * mm, "end": v(0, 1.19) * mm, "construction": true});
            skLineSegment(sketch, "E8.57.8.0", {"start": v(-9.2, 1.19) * mm, "end": v(-9.2, 0.39) * mm});
            skLineSegment(sketch, "E8.60.8.0", {"start": v(-6.4, 1.19) * mm, "end": v(-5.6, 1.19) * mm});
            skLineSegment(sketch, "E8.63.8.0", {"start": v(-7.6, 1.19) * mm, "end": v(-7.6, 0.39) * mm});
            skLineSegment(sketch, "E8.66.8.0", {"start": v(-6.8, 1.19) * mm, "end": v(-6.8, 0.39) * mm});
            skLineSegment(sketch, "E8.69.8.0", {"start": v(2.8, 1.19) * mm, "end": v(2.8, 0.39) * mm});
            skLineSegment(sketch, "E8.72.8.0", {"start": v(7.6, 1.19) * mm, "end": v(7.6, 0.39) * mm});
            skLineSegment(sketch, "E8.75.8.0", {"start": v(-2, 1.19) * mm, "end": v(-2, 0.39) * mm});
            skLineSegment(sketch, "E8.78.8.0", {"start": v(2, 1.19) * mm, "end": v(2.8, 1.19) * mm});
            skLineSegment(sketch, "E8.81.8.0", {"start": v(-4, 1.19) * mm, "end": v(-4, 0.39) * mm});
            skLineSegment(sketch, "E8.84.8.0", {"start": v(0.8, 1.19) * mm, "end": v(0.8, 0.39) * mm});
            skLineSegment(sketch, "E8.87.8.0", {"start": v(5.6, 1.19) * mm, "end": v(5.6, 0.39) * mm});
            skLineSegment(sketch, "E8.90.8.0", {"start": v(-3.2, 1.19) * mm, "end": v(-3.2, 0.39) * mm});
            skLineSegment(sketch, "E8.93.8.0", {"start": v(1.6, 1.19) * mm, "end": v(1.6, 0.39) * mm});
            skLineSegment(sketch, "E8.96.8.0", {"start": v(-4, 0.39) * mm, "end": v(-3.2, 0.39) * mm});
            skLineSegment(sketch, "E8.99.8.0", {"start": v(0.8, 0.39) * mm, "end": v(1.6, 0.39) * mm});
            skLineSegment(sketch, "E8.102.8.0", {"start": v(0.8, 1.19) * mm, "end": v(1.6, 1.19) * mm});
            skLineSegment(sketch, "E8.105.8.0", {"start": v(-10, 0.39) * mm, "end": v(-8.8, 0.39) * mm, "construction": true});
            skLineSegment(sketch, "E8.108.8.0", {"start": v(4.4, 1.19) * mm, "end": v(4.4, 0.39) * mm});
            skLineSegment(sketch, "E8.111.8.0", {"start": v(9.2, 1.19) * mm, "end": v(9.2, 0.39) * mm});
            skLineSegment(sketch, "E8.114.8.0", {"start": v(-5.2, 1.19) * mm, "end": v(-5.2, 0.39) * mm});
            skLineSegment(sketch, "E8.117.8.0", {"start": v(-0.4, 1.19) * mm, "end": v(-0.4, 0.39) * mm});
            skLineSegment(sketch, "E8.120.8.0", {"start": v(5.2, 1.19) * mm, "end": v(5.2, 0.39) * mm});
            skLineSegment(sketch, "E8.123.8.0", {"start": v(-4.4, 1.19) * mm, "end": v(-4.4, 0.39) * mm});
            skLineSegment(sketch, "E8.126.8.0", {"start": v(0.4, 1.19) * mm, "end": v(0.4, 0.39) * mm});
            skLineSegment(sketch, "E8.129.8.0", {"start": v(4.4, 0.39) * mm, "end": v(5.2, 0.39) * mm});
            skLineSegment(sketch, "E8.132.8.0", {"start": v(-5.2, 0.39) * mm, "end": v(-4.4, 0.39) * mm});
            skLineSegment(sketch, "E8.135.8.0", {"start": v(-0.4, 0.39) * mm, "end": v(0.4, 0.39) * mm});
            skLineSegment(sketch, "E8.138.8.0", {"start": v(4.4, 1.19) * mm, "end": v(5.2, 1.19) * mm});
            skLineSegment(sketch, "E8.141.8.0", {"start": v(-0.4, 1.19) * mm, "end": v(0.4, 1.19) * mm});
            skLineSegment(sketch, "E8.144.8.0", {"start": v(3.2, 1.19) * mm, "end": v(3.2, 0.39) * mm});
            skLineSegment(sketch, "E8.147.8.0", {"start": v(8, 1.19) * mm, "end": v(8, 0.39) * mm});
            skLineSegment(sketch, "E8.150.8.0", {"start": v(-6.4, 1.19) * mm, "end": v(-6.4, 0.39) * mm});
            skLineSegment(sketch, "E8.153.8.0", {"start": v(-1.6, 1.19) * mm, "end": v(-1.6, 0.39) * mm});
            skLineSegment(sketch, "E8.156.8.0", {"start": v(-5.6, 1.19) * mm, "end": v(-5.6, 0.39) * mm});
            skLineSegment(sketch, "E8.159.8.0", {"start": v(-0.8, 1.19) * mm, "end": v(-0.8, 0.39) * mm});
            skLineSegment(sketch, "E8.162.8.0", {"start": v(4, 1.19) * mm, "end": v(4, 0.39) * mm});
            skLineSegment(sketch, "E8.165.8.0", {"start": v(8.8, 1.19) * mm, "end": v(8.8, 0.39) * mm});
            skLineSegment(sketch, "E8.168.8.0", {"start": v(3.2, 0.39) * mm, "end": v(4, 0.39) * mm});
            skLineSegment(sketch, "E8.171.8.0", {"start": v(8, 0.39) * mm, "end": v(8.8, 0.39) * mm});
            skLineSegment(sketch, "E8.174.8.0", {"start": v(-6.4, 0.39) * mm, "end": v(-5.6, 0.39) * mm});
            skLineSegment(sketch, "E8.177.8.0", {"start": v(-1.6, 0.39) * mm, "end": v(-0.8, 0.39) * mm});
            skLineSegment(sketch, "E8.180.8.0", {"start": v(3.2, 1.19) * mm, "end": v(4, 1.19) * mm});
            skLineSegment(sketch, "E8.183.8.0", {"start": v(8, 1.19) * mm, "end": v(8.8, 1.19) * mm});
            skLineSegment(sketch, "E8.186.8.0", {"start": v(-8.8, 1.19) * mm, "end": v(-8, 1.19) * mm});
            skLineSegment(sketch, "E8.189.8.0", {"start": v(-10, 1.19) * mm, "end": v(-10, 0.39) * mm});
            skLineSegment(sketch, "E8.192.8.0", {"start": v(-10, 0.39) * mm, "end": v(-9.2, 0.39) * mm});
            skLineSegment(sketch, "E8.195.8.0", {"start": v(-10, 1.19) * mm, "end": v(-9.2, 1.19) * mm});
            skLineSegment(sketch, "E8.198.8.0", {"start": v(-2.8, 1.19) * mm, "end": v(-2, 1.19) * mm});
            skLineSegment(sketch, "E8.201.8.0", {"start": v(-4, 1.19) * mm, "end": v(-3.2, 1.19) * mm});
            skLineSegment(sketch, "E8.204.8.0", {"start": v(-5.2, 1.19) * mm, "end": v(-4.4, 1.19) * mm});
            skLineSegment(sketch, "E8.207.8.0", {"start": v(-1.6, 1.19) * mm, "end": v(-0.8, 1.19) * mm});
            skLineSegment(sketch, "E8.0.9.0", {"start": v(6.8, -0.01) * mm, "end": v(6.8, -0.81) * mm});
            skLineSegment(sketch, "E8.3.9.0", {"start": v(6.8, -0.81) * mm, "end": v(7.6, -0.81) * mm});
            skLineSegment(sketch, "E8.6.9.0", {"start": v(6.8, -0.01) * mm, "end": v(7.6, -0.01) * mm});
            skLineSegment(sketch, "E8.9.9.0", {"start": v(6.4, -0.01) * mm, "end": v(6.4, -0.81) * mm});
            skLineSegment(sketch, "E8.12.9.0", {"start": v(5.6, -0.81) * mm, "end": v(6.4, -0.81) * mm});
            skLineSegment(sketch, "E8.15.9.0", {"start": v(5.6, -0.01) * mm, "end": v(6.4, -0.01) * mm});
            skLineSegment(sketch, "E8.18.9.0", {"start": v(10, -0.01) * mm, "end": v(10, -0.81) * mm});
            skLineSegment(sketch, "E8.21.9.0", {"start": v(9.2, -0.81) * mm, "end": v(10, -0.81) * mm});
            skLineSegment(sketch, "E8.24.9.0", {"start": v(9.2, -0.01) * mm, "end": v(10, -0.01) * mm});
            skLineSegment(sketch, "E8.27.9.0", {"start": v(2, -0.01) * mm, "end": v(2, -0.81) * mm});
            skLineSegment(sketch, "E8.30.9.0", {"start": v(-2.8, -0.01) * mm, "end": v(-2.8, -0.81) * mm});
            skLineSegment(sketch, "E8.33.9.0", {"start": v(-7.6, -0.81) * mm, "end": v(-6.8, -0.81) * mm});
            skLineSegment(sketch, "E8.36.9.0", {"start": v(-7.6, -0.01) * mm, "end": v(-6.8, -0.01) * mm});
            skLineSegment(sketch, "E8.39.9.0", {"start": v(-2.8, -0.81) * mm, "end": v(-2, -0.81) * mm});
            skLineSegment(sketch, "E8.42.9.0", {"start": v(2, -0.81) * mm, "end": v(2.8, -0.81) * mm});
            skLineSegment(sketch, "E8.45.9.0", {"start": v(-8.8, -0.01) * mm, "end": v(-8.8, -0.81) * mm});
            skLineSegment(sketch, "E8.48.9.0", {"start": v(-8, -0.01) * mm, "end": v(-8, -0.81) * mm});
            skLineSegment(sketch, "E8.51.9.0", {"start": v(-8.8, -0.81) * mm, "end": v(-8, -0.81) * mm});
            skLineSegment(sketch, "E8.54.9.0", {"start": v(-10, -0.01) * mm, "end": v(0, -0.01) * mm, "construction": true});
            skLineSegment(sketch, "E8.57.9.0", {"start": v(-9.2, -0.01) * mm, "end": v(-9.2, -0.81) * mm});
            skLineSegment(sketch, "E8.60.9.0", {"start": v(-6.4, -0.01) * mm, "end": v(-5.6, -0.01) * mm});
            skLineSegment(sketch, "E8.63.9.0", {"start": v(-7.6, -0.01) * mm, "end": v(-7.6, -0.81) * mm});
            skLineSegment(sketch, "E8.66.9.0", {"start": v(-6.8, -0.01) * mm, "end": v(-6.8, -0.81) * mm});
            skLineSegment(sketch, "E8.69.9.0", {"start": v(2.8, -0.01) * mm, "end": v(2.8, -0.81) * mm});
            skLineSegment(sketch, "E8.72.9.0", {"start": v(7.6, -0.01) * mm, "end": v(7.6, -0.81) * mm});
            skLineSegment(sketch, "E8.75.9.0", {"start": v(-2, -0.01) * mm, "end": v(-2, -0.81) * mm});
            skLineSegment(sketch, "E8.78.9.0", {"start": v(2, -0.01) * mm, "end": v(2.8, -0.01) * mm});
            skLineSegment(sketch, "E8.81.9.0", {"start": v(-4, -0.01) * mm, "end": v(-4, -0.81) * mm});
            skLineSegment(sketch, "E8.84.9.0", {"start": v(0.8, -0.01) * mm, "end": v(0.8, -0.81) * mm});
            skLineSegment(sketch, "E8.87.9.0", {"start": v(5.6, -0.01) * mm, "end": v(5.6, -0.81) * mm});
            skLineSegment(sketch, "E8.90.9.0", {"start": v(-3.2, -0.01) * mm, "end": v(-3.2, -0.81) * mm});
            skLineSegment(sketch, "E8.93.9.0", {"start": v(1.6, -0.01) * mm, "end": v(1.6, -0.81) * mm});
            skLineSegment(sketch, "E8.96.9.0", {"start": v(-4, -0.81) * mm, "end": v(-3.2, -0.81) * mm});
            skLineSegment(sketch, "E8.99.9.0", {"start": v(0.8, -0.81) * mm, "end": v(1.6, -0.81) * mm});
            skLineSegment(sketch, "E8.102.9.0", {"start": v(0.8, -0.01) * mm, "end": v(1.6, -0.01) * mm});
            skLineSegment(sketch, "E8.105.9.0", {"start": v(-10, -0.81) * mm, "end": v(-8.8, -0.81) * mm, "construction": true});
            skLineSegment(sketch, "E8.108.9.0", {"start": v(4.4, -0.01) * mm, "end": v(4.4, -0.81) * mm});
            skLineSegment(sketch, "E8.111.9.0", {"start": v(9.2, -0.01) * mm, "end": v(9.2, -0.81) * mm});
            skLineSegment(sketch, "E8.114.9.0", {"start": v(-5.2, -0.01) * mm, "end": v(-5.2, -0.81) * mm});
            skLineSegment(sketch, "E8.117.9.0", {"start": v(-0.4, -0.01) * mm, "end": v(-0.4, -0.81) * mm});
            skLineSegment(sketch, "E8.120.9.0", {"start": v(5.2, -0.01) * mm, "end": v(5.2, -0.81) * mm});
            skLineSegment(sketch, "E8.123.9.0", {"start": v(-4.4, -0.01) * mm, "end": v(-4.4, -0.81) * mm});
            skLineSegment(sketch, "E8.126.9.0", {"start": v(0.4, -0.01) * mm, "end": v(0.4, -0.81) * mm});
            skLineSegment(sketch, "E8.129.9.0", {"start": v(4.4, -0.81) * mm, "end": v(5.2, -0.81) * mm});
            skLineSegment(sketch, "E8.132.9.0", {"start": v(-5.2, -0.81) * mm, "end": v(-4.4, -0.81) * mm});
            skLineSegment(sketch, "E8.135.9.0", {"start": v(-0.4, -0.81) * mm, "end": v(0.4, -0.81) * mm});
            skLineSegment(sketch, "E8.138.9.0", {"start": v(4.4, -0.01) * mm, "end": v(5.2, -0.01) * mm});
            skLineSegment(sketch, "E8.141.9.0", {"start": v(-0.4, -0.01) * mm, "end": v(0.4, -0.01) * mm});
            skLineSegment(sketch, "E8.144.9.0", {"start": v(3.2, -0.01) * mm, "end": v(3.2, -0.81) * mm});
            skLineSegment(sketch, "E8.147.9.0", {"start": v(8, -0.01) * mm, "end": v(8, -0.81) * mm});
            skLineSegment(sketch, "E8.150.9.0", {"start": v(-6.4, -0.01) * mm, "end": v(-6.4, -0.81) * mm});
            skLineSegment(sketch, "E8.153.9.0", {"start": v(-1.6, -0.01) * mm, "end": v(-1.6, -0.81) * mm});
            skLineSegment(sketch, "E8.156.9.0", {"start": v(-5.6, -0.01) * mm, "end": v(-5.6, -0.81) * mm});
            skLineSegment(sketch, "E8.159.9.0", {"start": v(-0.8, -0.01) * mm, "end": v(-0.8, -0.81) * mm});
            skLineSegment(sketch, "E8.162.9.0", {"start": v(4, -0.01) * mm, "end": v(4, -0.81) * mm});
            skLineSegment(sketch, "E8.165.9.0", {"start": v(8.8, -0.01) * mm, "end": v(8.8, -0.81) * mm});
            skLineSegment(sketch, "E8.168.9.0", {"start": v(3.2, -0.81) * mm, "end": v(4, -0.81) * mm});
            skLineSegment(sketch, "E8.171.9.0", {"start": v(8, -0.81) * mm, "end": v(8.8, -0.81) * mm});
            skLineSegment(sketch, "E8.174.9.0", {"start": v(-6.4, -0.81) * mm, "end": v(-5.6, -0.81) * mm});
            skLineSegment(sketch, "E8.177.9.0", {"start": v(-1.6, -0.81) * mm, "end": v(-0.8, -0.81) * mm});
            skLineSegment(sketch, "E8.180.9.0", {"start": v(3.2, -0.01) * mm, "end": v(4, -0.01) * mm});
            skLineSegment(sketch, "E8.183.9.0", {"start": v(8, -0.01) * mm, "end": v(8.8, -0.01) * mm});
            skLineSegment(sketch, "E8.186.9.0", {"start": v(-8.8, -0.01) * mm, "end": v(-8, -0.01) * mm});
            skLineSegment(sketch, "E8.189.9.0", {"start": v(-10, -0.01) * mm, "end": v(-10, -0.81) * mm});
            skLineSegment(sketch, "E8.192.9.0", {"start": v(-10, -0.81) * mm, "end": v(-9.2, -0.81) * mm});
            skLineSegment(sketch, "E8.195.9.0", {"start": v(-10, -0.01) * mm, "end": v(-9.2, -0.01) * mm});
            skLineSegment(sketch, "E8.198.9.0", {"start": v(-2.8, -0.01) * mm, "end": v(-2, -0.01) * mm});
            skLineSegment(sketch, "E8.201.9.0", {"start": v(-4, -0.01) * mm, "end": v(-3.2, -0.01) * mm});
            skLineSegment(sketch, "E8.204.9.0", {"start": v(-5.2, -0.01) * mm, "end": v(-4.4, -0.01) * mm});
            skLineSegment(sketch, "E8.207.9.0", {"start": v(-1.6, -0.01) * mm, "end": v(-0.8, -0.01) * mm});
            skLineSegment(sketch, "E8.0.10.0", {"start": v(6.8, -1.21) * mm, "end": v(6.8, -2.01) * mm});
            skLineSegment(sketch, "E8.3.10.0", {"start": v(6.8, -2.01) * mm, "end": v(7.6, -2.01) * mm});
            skLineSegment(sketch, "E8.6.10.0", {"start": v(6.8, -1.21) * mm, "end": v(7.6, -1.21) * mm});
            skLineSegment(sketch, "E8.9.10.0", {"start": v(6.4, -1.21) * mm, "end": v(6.4, -2.01) * mm});
            skLineSegment(sketch, "E8.12.10.0", {"start": v(5.6, -2.01) * mm, "end": v(6.4, -2.01) * mm});
            skLineSegment(sketch, "E8.15.10.0", {"start": v(5.6, -1.21) * mm, "end": v(6.4, -1.21) * mm});
            skLineSegment(sketch, "E8.18.10.0", {"start": v(10, -1.21) * mm, "end": v(10, -2.01) * mm});
            skLineSegment(sketch, "E8.21.10.0", {"start": v(9.2, -2.01) * mm, "end": v(10, -2.01) * mm});
            skLineSegment(sketch, "E8.24.10.0", {"start": v(9.2, -1.21) * mm, "end": v(10, -1.21) * mm});
            skLineSegment(sketch, "E8.27.10.0", {"start": v(2, -1.21) * mm, "end": v(2, -2.01) * mm});
            skLineSegment(sketch, "E8.30.10.0", {"start": v(-2.8, -1.21) * mm, "end": v(-2.8, -2.01) * mm});
            skLineSegment(sketch, "E8.33.10.0", {"start": v(-7.6, -2.01) * mm, "end": v(-6.8, -2.01) * mm});
            skLineSegment(sketch, "E8.36.10.0", {"start": v(-7.6, -1.21) * mm, "end": v(-6.8, -1.21) * mm});
            skLineSegment(sketch, "E8.39.10.0", {"start": v(-2.8, -2.01) * mm, "end": v(-2, -2.01) * mm});
            skLineSegment(sketch, "E8.42.10.0", {"start": v(2, -2.01) * mm, "end": v(2.8, -2.01) * mm});
            skLineSegment(sketch, "E8.45.10.0", {"start": v(-8.8, -1.21) * mm, "end": v(-8.8, -2.01) * mm});
            skLineSegment(sketch, "E8.48.10.0", {"start": v(-8, -1.21) * mm, "end": v(-8, -2.01) * mm});
            skLineSegment(sketch, "E8.51.10.0", {"start": v(-8.8, -2.01) * mm, "end": v(-8, -2.01) * mm});
            skLineSegment(sketch, "E8.54.10.0", {"start": v(-10, -1.21) * mm, "end": v(0, -1.21) * mm, "construction": true});
            skLineSegment(sketch, "E8.57.10.0", {"start": v(-9.2, -1.21) * mm, "end": v(-9.2, -2.01) * mm});
            skLineSegment(sketch, "E8.60.10.0", {"start": v(-6.4, -1.21) * mm, "end": v(-5.6, -1.21) * mm});
            skLineSegment(sketch, "E8.63.10.0", {"start": v(-7.6, -1.21) * mm, "end": v(-7.6, -2.01) * mm});
            skLineSegment(sketch, "E8.66.10.0", {"start": v(-6.8, -1.21) * mm, "end": v(-6.8, -2.01) * mm});
            skLineSegment(sketch, "E8.69.10.0", {"start": v(2.8, -1.21) * mm, "end": v(2.8, -2.01) * mm});
            skLineSegment(sketch, "E8.72.10.0", {"start": v(7.6, -1.21) * mm, "end": v(7.6, -2.01) * mm});
            skLineSegment(sketch, "E8.75.10.0", {"start": v(-2, -1.21) * mm, "end": v(-2, -2.01) * mm});
            skLineSegment(sketch, "E8.78.10.0", {"start": v(2, -1.21) * mm, "end": v(2.8, -1.21) * mm});
            skLineSegment(sketch, "E8.81.10.0", {"start": v(-4, -1.21) * mm, "end": v(-4, -2.01) * mm});
            skLineSegment(sketch, "E8.84.10.0", {"start": v(0.8, -1.21) * mm, "end": v(0.8, -2.01) * mm});
            skLineSegment(sketch, "E8.87.10.0", {"start": v(5.6, -1.21) * mm, "end": v(5.6, -2.01) * mm});
            skLineSegment(sketch, "E8.90.10.0", {"start": v(-3.2, -1.21) * mm, "end": v(-3.2, -2.01) * mm});
            skLineSegment(sketch, "E8.93.10.0", {"start": v(1.6, -1.21) * mm, "end": v(1.6, -2.01) * mm});
            skLineSegment(sketch, "E8.96.10.0", {"start": v(-4, -2.01) * mm, "end": v(-3.2, -2.01) * mm});
            skLineSegment(sketch, "E8.99.10.0", {"start": v(0.8, -2.01) * mm, "end": v(1.6, -2.01) * mm});
            skLineSegment(sketch, "E8.102.10.0", {"start": v(0.8, -1.21) * mm, "end": v(1.6, -1.21) * mm});
            skLineSegment(sketch, "E8.105.10.0", {"start": v(-10, -2.01) * mm, "end": v(-8.8, -2.01) * mm, "construction": true});
            skLineSegment(sketch, "E8.108.10.0", {"start": v(4.4, -1.21) * mm, "end": v(4.4, -2.01) * mm});
            skLineSegment(sketch, "E8.111.10.0", {"start": v(9.2, -1.21) * mm, "end": v(9.2, -2.01) * mm});
            skLineSegment(sketch, "E8.114.10.0", {"start": v(-5.2, -1.21) * mm, "end": v(-5.2, -2.01) * mm});
            skLineSegment(sketch, "E8.117.10.0", {"start": v(-0.4, -1.21) * mm, "end": v(-0.4, -2.01) * mm});
            skLineSegment(sketch, "E8.120.10.0", {"start": v(5.2, -1.21) * mm, "end": v(5.2, -2.01) * mm});
            skLineSegment(sketch, "E8.123.10.0", {"start": v(-4.4, -1.21) * mm, "end": v(-4.4, -2.01) * mm});
            skLineSegment(sketch, "E8.126.10.0", {"start": v(0.4, -1.21) * mm, "end": v(0.4, -2.01) * mm});
            skLineSegment(sketch, "E8.129.10.0", {"start": v(4.4, -2.01) * mm, "end": v(5.2, -2.01) * mm});
            skLineSegment(sketch, "E8.132.10.0", {"start": v(-5.2, -2.01) * mm, "end": v(-4.4, -2.01) * mm});
            skLineSegment(sketch, "E8.135.10.0", {"start": v(-0.4, -2.01) * mm, "end": v(0.4, -2.01) * mm});
            skLineSegment(sketch, "E8.138.10.0", {"start": v(4.4, -1.21) * mm, "end": v(5.2, -1.21) * mm});
            skLineSegment(sketch, "E8.141.10.0", {"start": v(-0.4, -1.21) * mm, "end": v(0.4, -1.21) * mm});
            skLineSegment(sketch, "E8.144.10.0", {"start": v(3.2, -1.21) * mm, "end": v(3.2, -2.01) * mm});
            skLineSegment(sketch, "E8.147.10.0", {"start": v(8, -1.21) * mm, "end": v(8, -2.01) * mm});
            skLineSegment(sketch, "E8.150.10.0", {"start": v(-6.4, -1.21) * mm, "end": v(-6.4, -2.01) * mm});
            skLineSegment(sketch, "E8.153.10.0", {"start": v(-1.6, -1.21) * mm, "end": v(-1.6, -2.01) * mm});
            skLineSegment(sketch, "E8.156.10.0", {"start": v(-5.6, -1.21) * mm, "end": v(-5.6, -2.01) * mm});
            skLineSegment(sketch, "E8.159.10.0", {"start": v(-0.8, -1.21) * mm, "end": v(-0.8, -2.01) * mm});
            skLineSegment(sketch, "E8.162.10.0", {"start": v(4, -1.21) * mm, "end": v(4, -2.01) * mm});
            skLineSegment(sketch, "E8.165.10.0", {"start": v(8.8, -1.21) * mm, "end": v(8.8, -2.01) * mm});
            skLineSegment(sketch, "E8.168.10.0", {"start": v(3.2, -2.01) * mm, "end": v(4, -2.01) * mm});
            skLineSegment(sketch, "E8.171.10.0", {"start": v(8, -2.01) * mm, "end": v(8.8, -2.01) * mm});
            skLineSegment(sketch, "E8.174.10.0", {"start": v(-6.4, -2.01) * mm, "end": v(-5.6, -2.01) * mm});
            skLineSegment(sketch, "E8.177.10.0", {"start": v(-1.6, -2.01) * mm, "end": v(-0.8, -2.01) * mm});
            skLineSegment(sketch, "E8.180.10.0", {"start": v(3.2, -1.21) * mm, "end": v(4, -1.21) * mm});
            skLineSegment(sketch, "E8.183.10.0", {"start": v(8, -1.21) * mm, "end": v(8.8, -1.21) * mm});
            skLineSegment(sketch, "E8.186.10.0", {"start": v(-8.8, -1.21) * mm, "end": v(-8, -1.21) * mm});
            skLineSegment(sketch, "E8.189.10.0", {"start": v(-10, -1.21) * mm, "end": v(-10, -2.01) * mm});
            skLineSegment(sketch, "E8.192.10.0", {"start": v(-10, -2.01) * mm, "end": v(-9.2, -2.01) * mm});
            skLineSegment(sketch, "E8.195.10.0", {"start": v(-10, -1.21) * mm, "end": v(-9.2, -1.21) * mm});
            skLineSegment(sketch, "E8.198.10.0", {"start": v(-2.8, -1.21) * mm, "end": v(-2, -1.21) * mm});
            skLineSegment(sketch, "E8.201.10.0", {"start": v(-4, -1.21) * mm, "end": v(-3.2, -1.21) * mm});
            skLineSegment(sketch, "E8.204.10.0", {"start": v(-5.2, -1.21) * mm, "end": v(-4.4, -1.21) * mm});
            skLineSegment(sketch, "E8.207.10.0", {"start": v(-1.6, -1.21) * mm, "end": v(-0.8, -1.21) * mm});
            skLineSegment(sketch, "E8.0.11.0", {"start": v(6.8, -2.41) * mm, "end": v(6.8, -3.21) * mm});
            skLineSegment(sketch, "E8.3.11.0", {"start": v(6.8, -3.21) * mm, "end": v(7.6, -3.21) * mm});
            skLineSegment(sketch, "E8.6.11.0", {"start": v(6.8, -2.41) * mm, "end": v(7.6, -2.41) * mm});
            skLineSegment(sketch, "E8.9.11.0", {"start": v(6.4, -2.41) * mm, "end": v(6.4, -3.21) * mm});
            skLineSegment(sketch, "E8.12.11.0", {"start": v(5.6, -3.21) * mm, "end": v(6.4, -3.21) * mm});
            skLineSegment(sketch, "E8.15.11.0", {"start": v(5.6, -2.41) * mm, "end": v(6.4, -2.41) * mm});
            skLineSegment(sketch, "E8.18.11.0", {"start": v(10, -2.41) * mm, "end": v(10, -3.21) * mm});
            skLineSegment(sketch, "E8.21.11.0", {"start": v(9.2, -3.21) * mm, "end": v(10, -3.21) * mm});
            skLineSegment(sketch, "E8.24.11.0", {"start": v(9.2, -2.41) * mm, "end": v(10, -2.41) * mm});
            skLineSegment(sketch, "E8.27.11.0", {"start": v(2, -2.41) * mm, "end": v(2, -3.21) * mm});
            skLineSegment(sketch, "E8.30.11.0", {"start": v(-2.8, -2.41) * mm, "end": v(-2.8, -3.21) * mm});
            skLineSegment(sketch, "E8.33.11.0", {"start": v(-7.6, -3.21) * mm, "end": v(-6.8, -3.21) * mm});
            skLineSegment(sketch, "E8.36.11.0", {"start": v(-7.6, -2.41) * mm, "end": v(-6.8, -2.41) * mm});
            skLineSegment(sketch, "E8.39.11.0", {"start": v(-2.8, -3.21) * mm, "end": v(-2, -3.21) * mm});
            skLineSegment(sketch, "E8.42.11.0", {"start": v(2, -3.21) * mm, "end": v(2.8, -3.21) * mm});
            skLineSegment(sketch, "E8.45.11.0", {"start": v(-8.8, -2.41) * mm, "end": v(-8.8, -3.21) * mm});
            skLineSegment(sketch, "E8.48.11.0", {"start": v(-8, -2.41) * mm, "end": v(-8, -3.21) * mm});
            skLineSegment(sketch, "E8.51.11.0", {"start": v(-8.8, -3.21) * mm, "end": v(-8, -3.21) * mm});
            skLineSegment(sketch, "E8.54.11.0", {"start": v(-10, -2.41) * mm, "end": v(0, -2.41) * mm, "construction": true});
            skLineSegment(sketch, "E8.57.11.0", {"start": v(-9.2, -2.41) * mm, "end": v(-9.2, -3.21) * mm});
            skLineSegment(sketch, "E8.60.11.0", {"start": v(-6.4, -2.41) * mm, "end": v(-5.6, -2.41) * mm});
            skLineSegment(sketch, "E8.63.11.0", {"start": v(-7.6, -2.41) * mm, "end": v(-7.6, -3.21) * mm});
            skLineSegment(sketch, "E8.66.11.0", {"start": v(-6.8, -2.41) * mm, "end": v(-6.8, -3.21) * mm});
            skLineSegment(sketch, "E8.69.11.0", {"start": v(2.8, -2.41) * mm, "end": v(2.8, -3.21) * mm});
            skLineSegment(sketch, "E8.72.11.0", {"start": v(7.6, -2.41) * mm, "end": v(7.6, -3.21) * mm});
            skLineSegment(sketch, "E8.75.11.0", {"start": v(-2, -2.41) * mm, "end": v(-2, -3.21) * mm});
            skLineSegment(sketch, "E8.78.11.0", {"start": v(2, -2.41) * mm, "end": v(2.8, -2.41) * mm});
            skLineSegment(sketch, "E8.81.11.0", {"start": v(-4, -2.41) * mm, "end": v(-4, -3.21) * mm});
            skLineSegment(sketch, "E8.84.11.0", {"start": v(0.8, -2.41) * mm, "end": v(0.8, -3.21) * mm});
            skLineSegment(sketch, "E8.87.11.0", {"start": v(5.6, -2.41) * mm, "end": v(5.6, -3.21) * mm});
            skLineSegment(sketch, "E8.90.11.0", {"start": v(-3.2, -2.41) * mm, "end": v(-3.2, -3.21) * mm});
            skLineSegment(sketch, "E8.93.11.0", {"start": v(1.6, -2.41) * mm, "end": v(1.6, -3.21) * mm});
            skLineSegment(sketch, "E8.96.11.0", {"start": v(-4, -3.21) * mm, "end": v(-3.2, -3.21) * mm});
            skLineSegment(sketch, "E8.99.11.0", {"start": v(0.8, -3.21) * mm, "end": v(1.6, -3.21) * mm});
            skLineSegment(sketch, "E8.102.11.0", {"start": v(0.8, -2.41) * mm, "end": v(1.6, -2.41) * mm});
            skLineSegment(sketch, "E8.105.11.0", {"start": v(-10, -3.21) * mm, "end": v(-8.8, -3.21) * mm, "construction": true});
            skLineSegment(sketch, "E8.108.11.0", {"start": v(4.4, -2.41) * mm, "end": v(4.4, -3.21) * mm});
            skLineSegment(sketch, "E8.111.11.0", {"start": v(9.2, -2.41) * mm, "end": v(9.2, -3.21) * mm});
            skLineSegment(sketch, "E8.114.11.0", {"start": v(-5.2, -2.41) * mm, "end": v(-5.2, -3.21) * mm});
            skLineSegment(sketch, "E8.117.11.0", {"start": v(-0.4, -2.41) * mm, "end": v(-0.4, -3.21) * mm});
            skLineSegment(sketch, "E8.120.11.0", {"start": v(5.2, -2.41) * mm, "end": v(5.2, -3.21) * mm});
            skLineSegment(sketch, "E8.123.11.0", {"start": v(-4.4, -2.41) * mm, "end": v(-4.4, -3.21) * mm});
            skLineSegment(sketch, "E8.126.11.0", {"start": v(0.4, -2.41) * mm, "end": v(0.4, -3.21) * mm});
            skLineSegment(sketch, "E8.129.11.0", {"start": v(4.4, -3.21) * mm, "end": v(5.2, -3.21) * mm});
            skLineSegment(sketch, "E8.132.11.0", {"start": v(-5.2, -3.21) * mm, "end": v(-4.4, -3.21) * mm});
            skLineSegment(sketch, "E8.135.11.0", {"start": v(-0.4, -3.21) * mm, "end": v(0.4, -3.21) * mm});
            skLineSegment(sketch, "E8.138.11.0", {"start": v(4.4, -2.41) * mm, "end": v(5.2, -2.41) * mm});
            skLineSegment(sketch, "E8.141.11.0", {"start": v(-0.4, -2.41) * mm, "end": v(0.4, -2.41) * mm});
            skLineSegment(sketch, "E8.144.11.0", {"start": v(3.2, -2.41) * mm, "end": v(3.2, -3.21) * mm});
            skLineSegment(sketch, "E8.147.11.0", {"start": v(8, -2.41) * mm, "end": v(8, -3.21) * mm});
            skLineSegment(sketch, "E8.150.11.0", {"start": v(-6.4, -2.41) * mm, "end": v(-6.4, -3.21) * mm});
            skLineSegment(sketch, "E8.153.11.0", {"start": v(-1.6, -2.41) * mm, "end": v(-1.6, -3.21) * mm});
            skLineSegment(sketch, "E8.156.11.0", {"start": v(-5.6, -2.41) * mm, "end": v(-5.6, -3.21) * mm});
            skLineSegment(sketch, "E8.159.11.0", {"start": v(-0.8, -2.41) * mm, "end": v(-0.8, -3.21) * mm});
            skLineSegment(sketch, "E8.162.11.0", {"start": v(4, -2.41) * mm, "end": v(4, -3.21) * mm});
            skLineSegment(sketch, "E8.165.11.0", {"start": v(8.8, -2.41) * mm, "end": v(8.8, -3.21) * mm});
            skLineSegment(sketch, "E8.168.11.0", {"start": v(3.2, -3.21) * mm, "end": v(4, -3.21) * mm});
            skLineSegment(sketch, "E8.171.11.0", {"start": v(8, -3.21) * mm, "end": v(8.8, -3.21) * mm});
            skLineSegment(sketch, "E8.174.11.0", {"start": v(-6.4, -3.21) * mm, "end": v(-5.6, -3.21) * mm});
            skLineSegment(sketch, "E8.177.11.0", {"start": v(-1.6, -3.21) * mm, "end": v(-0.8, -3.21) * mm});
            skLineSegment(sketch, "E8.180.11.0", {"start": v(3.2, -2.41) * mm, "end": v(4, -2.41) * mm});
            skLineSegment(sketch, "E8.183.11.0", {"start": v(8, -2.41) * mm, "end": v(8.8, -2.41) * mm});
            skLineSegment(sketch, "E8.186.11.0", {"start": v(-8.8, -2.41) * mm, "end": v(-8, -2.41) * mm});
            skLineSegment(sketch, "E8.189.11.0", {"start": v(-10, -2.41) * mm, "end": v(-10, -3.21) * mm});
            skLineSegment(sketch, "E8.192.11.0", {"start": v(-10, -3.21) * mm, "end": v(-9.2, -3.21) * mm});
            skLineSegment(sketch, "E8.195.11.0", {"start": v(-10, -2.41) * mm, "end": v(-9.2, -2.41) * mm});
            skLineSegment(sketch, "E8.198.11.0", {"start": v(-2.8, -2.41) * mm, "end": v(-2, -2.41) * mm});
            skLineSegment(sketch, "E8.201.11.0", {"start": v(-4, -2.41) * mm, "end": v(-3.2, -2.41) * mm});
            skLineSegment(sketch, "E8.204.11.0", {"start": v(-5.2, -2.41) * mm, "end": v(-4.4, -2.41) * mm});
            skLineSegment(sketch, "E8.207.11.0", {"start": v(-1.6, -2.41) * mm, "end": v(-0.8, -2.41) * mm});
            skLineSegment(sketch, "E8.0.12.0", {"start": v(6.8, -3.61) * mm, "end": v(6.8, -4.41) * mm});
            skLineSegment(sketch, "E8.3.12.0", {"start": v(6.8, -4.41) * mm, "end": v(7.6, -4.41) * mm});
            skLineSegment(sketch, "E8.6.12.0", {"start": v(6.8, -3.61) * mm, "end": v(7.6, -3.61) * mm});
            skLineSegment(sketch, "E8.9.12.0", {"start": v(6.4, -3.61) * mm, "end": v(6.4, -4.41) * mm});
            skLineSegment(sketch, "E8.12.12.0", {"start": v(5.6, -4.41) * mm, "end": v(6.4, -4.41) * mm});
            skLineSegment(sketch, "E8.15.12.0", {"start": v(5.6, -3.61) * mm, "end": v(6.4, -3.61) * mm});
            skLineSegment(sketch, "E8.18.12.0", {"start": v(10, -3.61) * mm, "end": v(10, -4.41) * mm});
            skLineSegment(sketch, "E8.21.12.0", {"start": v(9.2, -4.41) * mm, "end": v(10, -4.41) * mm});
            skLineSegment(sketch, "E8.24.12.0", {"start": v(9.2, -3.61) * mm, "end": v(10, -3.61) * mm});
            skLineSegment(sketch, "E8.27.12.0", {"start": v(2, -3.61) * mm, "end": v(2, -4.41) * mm});
            skLineSegment(sketch, "E8.30.12.0", {"start": v(-2.8, -3.61) * mm, "end": v(-2.8, -4.41) * mm});
            skLineSegment(sketch, "E8.33.12.0", {"start": v(-7.6, -4.41) * mm, "end": v(-6.8, -4.41) * mm});
            skLineSegment(sketch, "E8.36.12.0", {"start": v(-7.6, -3.61) * mm, "end": v(-6.8, -3.61) * mm});
            skLineSegment(sketch, "E8.39.12.0", {"start": v(-2.8, -4.41) * mm, "end": v(-2, -4.41) * mm});
            skLineSegment(sketch, "E8.42.12.0", {"start": v(2, -4.41) * mm, "end": v(2.8, -4.41) * mm});
            skLineSegment(sketch, "E8.45.12.0", {"start": v(-8.8, -3.61) * mm, "end": v(-8.8, -4.41) * mm});
            skLineSegment(sketch, "E8.48.12.0", {"start": v(-8, -3.61) * mm, "end": v(-8, -4.41) * mm});
            skLineSegment(sketch, "E8.51.12.0", {"start": v(-8.8, -4.41) * mm, "end": v(-8, -4.41) * mm});
            skLineSegment(sketch, "E8.54.12.0", {"start": v(-10, -3.61) * mm, "end": v(0, -3.61) * mm, "construction": true});
            skLineSegment(sketch, "E8.57.12.0", {"start": v(-9.2, -3.61) * mm, "end": v(-9.2, -4.41) * mm});
            skLineSegment(sketch, "E8.60.12.0", {"start": v(-6.4, -3.61) * mm, "end": v(-5.6, -3.61) * mm});
            skLineSegment(sketch, "E8.63.12.0", {"start": v(-7.6, -3.61) * mm, "end": v(-7.6, -4.41) * mm});
            skLineSegment(sketch, "E8.66.12.0", {"start": v(-6.8, -3.61) * mm, "end": v(-6.8, -4.41) * mm});
            skLineSegment(sketch, "E8.69.12.0", {"start": v(2.8, -3.61) * mm, "end": v(2.8, -4.41) * mm});
            skLineSegment(sketch, "E8.72.12.0", {"start": v(7.6, -3.61) * mm, "end": v(7.6, -4.41) * mm});
            skLineSegment(sketch, "E8.75.12.0", {"start": v(-2, -3.61) * mm, "end": v(-2, -4.41) * mm});
            skLineSegment(sketch, "E8.78.12.0", {"start": v(2, -3.61) * mm, "end": v(2.8, -3.61) * mm});
            skLineSegment(sketch, "E8.81.12.0", {"start": v(-4, -3.61) * mm, "end": v(-4, -4.41) * mm});
            skLineSegment(sketch, "E8.84.12.0", {"start": v(0.8, -3.61) * mm, "end": v(0.8, -4.41) * mm});
            skLineSegment(sketch, "E8.87.12.0", {"start": v(5.6, -3.61) * mm, "end": v(5.6, -4.41) * mm});
            skLineSegment(sketch, "E8.90.12.0", {"start": v(-3.2, -3.61) * mm, "end": v(-3.2, -4.41) * mm});
            skLineSegment(sketch, "E8.93.12.0", {"start": v(1.6, -3.61) * mm, "end": v(1.6, -4.41) * mm});
            skLineSegment(sketch, "E8.96.12.0", {"start": v(-4, -4.41) * mm, "end": v(-3.2, -4.41) * mm});
            skLineSegment(sketch, "E8.99.12.0", {"start": v(0.8, -4.41) * mm, "end": v(1.6, -4.41) * mm});
            skLineSegment(sketch, "E8.102.12.0", {"start": v(0.8, -3.61) * mm, "end": v(1.6, -3.61) * mm});
            skLineSegment(sketch, "E8.105.12.0", {"start": v(-10, -4.41) * mm, "end": v(-8.8, -4.41) * mm, "construction": true});
            skLineSegment(sketch, "E8.108.12.0", {"start": v(4.4, -3.61) * mm, "end": v(4.4, -4.41) * mm});
            skLineSegment(sketch, "E8.111.12.0", {"start": v(9.2, -3.61) * mm, "end": v(9.2, -4.41) * mm});
            skLineSegment(sketch, "E8.114.12.0", {"start": v(-5.2, -3.61) * mm, "end": v(-5.2, -4.41) * mm});
            skLineSegment(sketch, "E8.117.12.0", {"start": v(-0.4, -3.61) * mm, "end": v(-0.4, -4.41) * mm});
            skLineSegment(sketch, "E8.120.12.0", {"start": v(5.2, -3.61) * mm, "end": v(5.2, -4.41) * mm});
            skLineSegment(sketch, "E8.123.12.0", {"start": v(-4.4, -3.61) * mm, "end": v(-4.4, -4.41) * mm});
            skLineSegment(sketch, "E8.126.12.0", {"start": v(0.4, -3.61) * mm, "end": v(0.4, -4.41) * mm});
            skLineSegment(sketch, "E8.129.12.0", {"start": v(4.4, -4.41) * mm, "end": v(5.2, -4.41) * mm});
            skLineSegment(sketch, "E8.132.12.0", {"start": v(-5.2, -4.41) * mm, "end": v(-4.4, -4.41) * mm});
            skLineSegment(sketch, "E8.135.12.0", {"start": v(-0.4, -4.41) * mm, "end": v(0.4, -4.41) * mm});
            skLineSegment(sketch, "E8.138.12.0", {"start": v(4.4, -3.61) * mm, "end": v(5.2, -3.61) * mm});
            skLineSegment(sketch, "E8.141.12.0", {"start": v(-0.4, -3.61) * mm, "end": v(0.4, -3.61) * mm});
            skLineSegment(sketch, "E8.144.12.0", {"start": v(3.2, -3.61) * mm, "end": v(3.2, -4.41) * mm});
            skLineSegment(sketch, "E8.147.12.0", {"start": v(8, -3.61) * mm, "end": v(8, -4.41) * mm});
            skLineSegment(sketch, "E8.150.12.0", {"start": v(-6.4, -3.61) * mm, "end": v(-6.4, -4.41) * mm});
            skLineSegment(sketch, "E8.153.12.0", {"start": v(-1.6, -3.61) * mm, "end": v(-1.6, -4.41) * mm});
            skLineSegment(sketch, "E8.156.12.0", {"start": v(-5.6, -3.61) * mm, "end": v(-5.6, -4.41) * mm});
            skLineSegment(sketch, "E8.159.12.0", {"start": v(-0.8, -3.61) * mm, "end": v(-0.8, -4.41) * mm});
            skLineSegment(sketch, "E8.162.12.0", {"start": v(4, -3.61) * mm, "end": v(4, -4.41) * mm});
            skLineSegment(sketch, "E8.165.12.0", {"start": v(8.8, -3.61) * mm, "end": v(8.8, -4.41) * mm});
            skLineSegment(sketch, "E8.168.12.0", {"start": v(3.2, -4.41) * mm, "end": v(4, -4.41) * mm});
            skLineSegment(sketch, "E8.171.12.0", {"start": v(8, -4.41) * mm, "end": v(8.8, -4.41) * mm});
            skLineSegment(sketch, "E8.174.12.0", {"start": v(-6.4, -4.41) * mm, "end": v(-5.6, -4.41) * mm});
            skLineSegment(sketch, "E8.177.12.0", {"start": v(-1.6, -4.41) * mm, "end": v(-0.8, -4.41) * mm});
            skLineSegment(sketch, "E8.180.12.0", {"start": v(3.2, -3.61) * mm, "end": v(4, -3.61) * mm});
            skLineSegment(sketch, "E8.183.12.0", {"start": v(8, -3.61) * mm, "end": v(8.8, -3.61) * mm});
            skLineSegment(sketch, "E8.186.12.0", {"start": v(-8.8, -3.61) * mm, "end": v(-8, -3.61) * mm});
            skLineSegment(sketch, "E8.189.12.0", {"start": v(-10, -3.61) * mm, "end": v(-10, -4.41) * mm});
            skLineSegment(sketch, "E8.192.12.0", {"start": v(-10, -4.41) * mm, "end": v(-9.2, -4.41) * mm});
            skLineSegment(sketch, "E8.195.12.0", {"start": v(-10, -3.61) * mm, "end": v(-9.2, -3.61) * mm});
            skLineSegment(sketch, "E8.198.12.0", {"start": v(-2.8, -3.61) * mm, "end": v(-2, -3.61) * mm});
            skLineSegment(sketch, "E8.201.12.0", {"start": v(-4, -3.61) * mm, "end": v(-3.2, -3.61) * mm});
            skLineSegment(sketch, "E8.204.12.0", {"start": v(-5.2, -3.61) * mm, "end": v(-4.4, -3.61) * mm});
            skLineSegment(sketch, "E8.207.12.0", {"start": v(-1.6, -3.61) * mm, "end": v(-0.8, -3.61) * mm});
            skLineSegment(sketch, "E8.0.13.0", {"start": v(6.8, -4.81) * mm, "end": v(6.8, -5.61) * mm});
            skLineSegment(sketch, "E8.3.13.0", {"start": v(6.8, -5.61) * mm, "end": v(7.6, -5.61) * mm});
            skLineSegment(sketch, "E8.6.13.0", {"start": v(6.8, -4.81) * mm, "end": v(7.6, -4.81) * mm});
            skLineSegment(sketch, "E8.9.13.0", {"start": v(6.4, -4.81) * mm, "end": v(6.4, -5.61) * mm});
            skLineSegment(sketch, "E8.12.13.0", {"start": v(5.6, -5.61) * mm, "end": v(6.4, -5.61) * mm});
            skLineSegment(sketch, "E8.15.13.0", {"start": v(5.6, -4.81) * mm, "end": v(6.4, -4.81) * mm});
            skLineSegment(sketch, "E8.18.13.0", {"start": v(10, -4.81) * mm, "end": v(10, -5.61) * mm});
            skLineSegment(sketch, "E8.21.13.0", {"start": v(9.2, -5.61) * mm, "end": v(10, -5.61) * mm});
            skLineSegment(sketch, "E8.24.13.0", {"start": v(9.2, -4.81) * mm, "end": v(10, -4.81) * mm});
            skLineSegment(sketch, "E8.27.13.0", {"start": v(2, -4.81) * mm, "end": v(2, -5.61) * mm});
            skLineSegment(sketch, "E8.30.13.0", {"start": v(-2.8, -4.81) * mm, "end": v(-2.8, -5.61) * mm});
            skLineSegment(sketch, "E8.33.13.0", {"start": v(-7.6, -5.61) * mm, "end": v(-6.8, -5.61) * mm});
            skLineSegment(sketch, "E8.36.13.0", {"start": v(-7.6, -4.81) * mm, "end": v(-6.8, -4.81) * mm});
            skLineSegment(sketch, "E8.39.13.0", {"start": v(-2.8, -5.61) * mm, "end": v(-2, -5.61) * mm});
            skLineSegment(sketch, "E8.42.13.0", {"start": v(2, -5.61) * mm, "end": v(2.8, -5.61) * mm});
            skLineSegment(sketch, "E8.45.13.0", {"start": v(-8.8, -4.81) * mm, "end": v(-8.8, -5.61) * mm});
            skLineSegment(sketch, "E8.48.13.0", {"start": v(-8, -4.81) * mm, "end": v(-8, -5.61) * mm});
            skLineSegment(sketch, "E8.51.13.0", {"start": v(-8.8, -5.61) * mm, "end": v(-8, -5.61) * mm});
            skLineSegment(sketch, "E8.54.13.0", {"start": v(-10, -4.81) * mm, "end": v(0, -4.81) * mm, "construction": true});
            skLineSegment(sketch, "E8.57.13.0", {"start": v(-9.2, -4.81) * mm, "end": v(-9.2, -5.61) * mm});
            skLineSegment(sketch, "E8.60.13.0", {"start": v(-6.4, -4.81) * mm, "end": v(-5.6, -4.81) * mm});
            skLineSegment(sketch, "E8.63.13.0", {"start": v(-7.6, -4.81) * mm, "end": v(-7.6, -5.61) * mm});
            skLineSegment(sketch, "E8.66.13.0", {"start": v(-6.8, -4.81) * mm, "end": v(-6.8, -5.61) * mm});
            skLineSegment(sketch, "E8.69.13.0", {"start": v(2.8, -4.81) * mm, "end": v(2.8, -5.61) * mm});
            skLineSegment(sketch, "E8.72.13.0", {"start": v(7.6, -4.81) * mm, "end": v(7.6, -5.61) * mm});
            skLineSegment(sketch, "E8.75.13.0", {"start": v(-2, -4.81) * mm, "end": v(-2, -5.61) * mm});
            skLineSegment(sketch, "E8.78.13.0", {"start": v(2, -4.81) * mm, "end": v(2.8, -4.81) * mm});
            skLineSegment(sketch, "E8.81.13.0", {"start": v(-4, -4.81) * mm, "end": v(-4, -5.61) * mm});
            skLineSegment(sketch, "E8.84.13.0", {"start": v(0.8, -4.81) * mm, "end": v(0.8, -5.61) * mm});
            skLineSegment(sketch, "E8.87.13.0", {"start": v(5.6, -4.81) * mm, "end": v(5.6, -5.61) * mm});
            skLineSegment(sketch, "E8.90.13.0", {"start": v(-3.2, -4.81) * mm, "end": v(-3.2, -5.61) * mm});
            skLineSegment(sketch, "E8.93.13.0", {"start": v(1.6, -4.81) * mm, "end": v(1.6, -5.61) * mm});
            skLineSegment(sketch, "E8.96.13.0", {"start": v(-4, -5.61) * mm, "end": v(-3.2, -5.61) * mm});
            skLineSegment(sketch, "E8.99.13.0", {"start": v(0.8, -5.61) * mm, "end": v(1.6, -5.61) * mm});
            skLineSegment(sketch, "E8.102.13.0", {"start": v(0.8, -4.81) * mm, "end": v(1.6, -4.81) * mm});
            skLineSegment(sketch, "E8.105.13.0", {"start": v(-10, -5.61) * mm, "end": v(-8.8, -5.61) * mm, "construction": true});
            skLineSegment(sketch, "E8.108.13.0", {"start": v(4.4, -4.81) * mm, "end": v(4.4, -5.61) * mm});
            skLineSegment(sketch, "E8.111.13.0", {"start": v(9.2, -4.81) * mm, "end": v(9.2, -5.61) * mm});
            skLineSegment(sketch, "E8.114.13.0", {"start": v(-5.2, -4.81) * mm, "end": v(-5.2, -5.61) * mm});
            skLineSegment(sketch, "E8.117.13.0", {"start": v(-0.4, -4.81) * mm, "end": v(-0.4, -5.61) * mm});
            skLineSegment(sketch, "E8.120.13.0", {"start": v(5.2, -4.81) * mm, "end": v(5.2, -5.61) * mm});
            skLineSegment(sketch, "E8.123.13.0", {"start": v(-4.4, -4.81) * mm, "end": v(-4.4, -5.61) * mm});
            skLineSegment(sketch, "E8.126.13.0", {"start": v(0.4, -4.81) * mm, "end": v(0.4, -5.61) * mm});
            skLineSegment(sketch, "E8.129.13.0", {"start": v(4.4, -5.61) * mm, "end": v(5.2, -5.61) * mm});
            skLineSegment(sketch, "E8.132.13.0", {"start": v(-5.2, -5.61) * mm, "end": v(-4.4, -5.61) * mm});
            skLineSegment(sketch, "E8.135.13.0", {"start": v(-0.4, -5.61) * mm, "end": v(0.4, -5.61) * mm});
            skLineSegment(sketch, "E8.138.13.0", {"start": v(4.4, -4.81) * mm, "end": v(5.2, -4.81) * mm});
            skLineSegment(sketch, "E8.141.13.0", {"start": v(-0.4, -4.81) * mm, "end": v(0.4, -4.81) * mm});
            skLineSegment(sketch, "E8.144.13.0", {"start": v(3.2, -4.81) * mm, "end": v(3.2, -5.61) * mm});
            skLineSegment(sketch, "E8.147.13.0", {"start": v(8, -4.81) * mm, "end": v(8, -5.61) * mm});
            skLineSegment(sketch, "E8.150.13.0", {"start": v(-6.4, -4.81) * mm, "end": v(-6.4, -5.61) * mm});
            skLineSegment(sketch, "E8.153.13.0", {"start": v(-1.6, -4.81) * mm, "end": v(-1.6, -5.61) * mm});
            skLineSegment(sketch, "E8.156.13.0", {"start": v(-5.6, -4.81) * mm, "end": v(-5.6, -5.61) * mm});
            skLineSegment(sketch, "E8.159.13.0", {"start": v(-0.8, -4.81) * mm, "end": v(-0.8, -5.61) * mm});
            skLineSegment(sketch, "E8.162.13.0", {"start": v(4, -4.81) * mm, "end": v(4, -5.61) * mm});
            skLineSegment(sketch, "E8.165.13.0", {"start": v(8.8, -4.81) * mm, "end": v(8.8, -5.61) * mm});
            skLineSegment(sketch, "E8.168.13.0", {"start": v(3.2, -5.61) * mm, "end": v(4, -5.61) * mm});
            skLineSegment(sketch, "E8.171.13.0", {"start": v(8, -5.61) * mm, "end": v(8.8, -5.61) * mm});
            skLineSegment(sketch, "E8.174.13.0", {"start": v(-6.4, -5.61) * mm, "end": v(-5.6, -5.61) * mm});
            skLineSegment(sketch, "E8.177.13.0", {"start": v(-1.6, -5.61) * mm, "end": v(-0.8, -5.61) * mm});
            skLineSegment(sketch, "E8.180.13.0", {"start": v(3.2, -4.81) * mm, "end": v(4, -4.81) * mm});
            skLineSegment(sketch, "E8.183.13.0", {"start": v(8, -4.81) * mm, "end": v(8.8, -4.81) * mm});
            skLineSegment(sketch, "E8.186.13.0", {"start": v(-8.8, -4.81) * mm, "end": v(-8, -4.81) * mm});
            skLineSegment(sketch, "E8.189.13.0", {"start": v(-10, -4.81) * mm, "end": v(-10, -5.61) * mm});
            skLineSegment(sketch, "E8.192.13.0", {"start": v(-10, -5.61) * mm, "end": v(-9.2, -5.61) * mm});
            skLineSegment(sketch, "E8.195.13.0", {"start": v(-10, -4.81) * mm, "end": v(-9.2, -4.81) * mm});
            skLineSegment(sketch, "E8.198.13.0", {"start": v(-2.8, -4.81) * mm, "end": v(-2, -4.81) * mm});
            skLineSegment(sketch, "E8.201.13.0", {"start": v(-4, -4.81) * mm, "end": v(-3.2, -4.81) * mm});
            skLineSegment(sketch, "E8.204.13.0", {"start": v(-5.2, -4.81) * mm, "end": v(-4.4, -4.81) * mm});
            skLineSegment(sketch, "E8.207.13.0", {"start": v(-1.6, -4.81) * mm, "end": v(-0.8, -4.81) * mm});
            skLineSegment(sketch, "E8.0.14.0", {"start": v(6.8, -6.01) * mm, "end": v(6.8, -6.81) * mm});
            skLineSegment(sketch, "E8.3.14.0", {"start": v(6.8, -6.81) * mm, "end": v(7.6, -6.81) * mm});
            skLineSegment(sketch, "E8.6.14.0", {"start": v(6.8, -6.01) * mm, "end": v(7.6, -6.01) * mm});
            skLineSegment(sketch, "E8.9.14.0", {"start": v(6.4, -6.01) * mm, "end": v(6.4, -6.81) * mm});
            skLineSegment(sketch, "E8.12.14.0", {"start": v(5.6, -6.81) * mm, "end": v(6.4, -6.81) * mm});
            skLineSegment(sketch, "E8.15.14.0", {"start": v(5.6, -6.01) * mm, "end": v(6.4, -6.01) * mm});
            skLineSegment(sketch, "E8.18.14.0", {"start": v(10, -6.01) * mm, "end": v(10, -6.81) * mm});
            skLineSegment(sketch, "E8.21.14.0", {"start": v(9.2, -6.81) * mm, "end": v(10, -6.81) * mm});
            skLineSegment(sketch, "E8.24.14.0", {"start": v(9.2, -6.01) * mm, "end": v(10, -6.01) * mm});
            skLineSegment(sketch, "E8.27.14.0", {"start": v(2, -6.01) * mm, "end": v(2, -6.81) * mm});
            skLineSegment(sketch, "E8.30.14.0", {"start": v(-2.8, -6.01) * mm, "end": v(-2.8, -6.81) * mm});
            skLineSegment(sketch, "E8.33.14.0", {"start": v(-7.6, -6.81) * mm, "end": v(-6.8, -6.81) * mm});
            skLineSegment(sketch, "E8.36.14.0", {"start": v(-7.6, -6.01) * mm, "end": v(-6.8, -6.01) * mm});
            skLineSegment(sketch, "E8.39.14.0", {"start": v(-2.8, -6.81) * mm, "end": v(-2, -6.81) * mm});
            skLineSegment(sketch, "E8.42.14.0", {"start": v(2, -6.81) * mm, "end": v(2.8, -6.81) * mm});
            skLineSegment(sketch, "E8.45.14.0", {"start": v(-8.8, -6.01) * mm, "end": v(-8.8, -6.81) * mm});
            skLineSegment(sketch, "E8.48.14.0", {"start": v(-8, -6.01) * mm, "end": v(-8, -6.81) * mm});
            skLineSegment(sketch, "E8.51.14.0", {"start": v(-8.8, -6.81) * mm, "end": v(-8, -6.81) * mm});
            skLineSegment(sketch, "E8.54.14.0", {"start": v(-10, -6.01) * mm, "end": v(0, -6.01) * mm, "construction": true});
            skLineSegment(sketch, "E8.57.14.0", {"start": v(-9.2, -6.01) * mm, "end": v(-9.2, -6.81) * mm});
            skLineSegment(sketch, "E8.60.14.0", {"start": v(-6.4, -6.01) * mm, "end": v(-5.6, -6.01) * mm});
            skLineSegment(sketch, "E8.63.14.0", {"start": v(-7.6, -6.01) * mm, "end": v(-7.6, -6.81) * mm});
            skLineSegment(sketch, "E8.66.14.0", {"start": v(-6.8, -6.01) * mm, "end": v(-6.8, -6.81) * mm});
            skLineSegment(sketch, "E8.69.14.0", {"start": v(2.8, -6.01) * mm, "end": v(2.8, -6.81) * mm});
            skLineSegment(sketch, "E8.72.14.0", {"start": v(7.6, -6.01) * mm, "end": v(7.6, -6.81) * mm});
            skLineSegment(sketch, "E8.75.14.0", {"start": v(-2, -6.01) * mm, "end": v(-2, -6.81) * mm});
            skLineSegment(sketch, "E8.78.14.0", {"start": v(2, -6.01) * mm, "end": v(2.8, -6.01) * mm});
            skLineSegment(sketch, "E8.81.14.0", {"start": v(-4, -6.01) * mm, "end": v(-4, -6.81) * mm});
            skLineSegment(sketch, "E8.84.14.0", {"start": v(0.8, -6.01) * mm, "end": v(0.8, -6.81) * mm});
            skLineSegment(sketch, "E8.87.14.0", {"start": v(5.6, -6.01) * mm, "end": v(5.6, -6.81) * mm});
            skLineSegment(sketch, "E8.90.14.0", {"start": v(-3.2, -6.01) * mm, "end": v(-3.2, -6.81) * mm});
            skLineSegment(sketch, "E8.93.14.0", {"start": v(1.6, -6.01) * mm, "end": v(1.6, -6.81) * mm});
            skLineSegment(sketch, "E8.96.14.0", {"start": v(-4, -6.81) * mm, "end": v(-3.2, -6.81) * mm});
            skLineSegment(sketch, "E8.99.14.0", {"start": v(0.8, -6.81) * mm, "end": v(1.6, -6.81) * mm});
            skLineSegment(sketch, "E8.102.14.0", {"start": v(0.8, -6.01) * mm, "end": v(1.6, -6.01) * mm});
            skLineSegment(sketch, "E8.105.14.0", {"start": v(-10, -6.81) * mm, "end": v(-8.8, -6.81) * mm, "construction": true});
            skLineSegment(sketch, "E8.108.14.0", {"start": v(4.4, -6.01) * mm, "end": v(4.4, -6.81) * mm});
            skLineSegment(sketch, "E8.111.14.0", {"start": v(9.2, -6.01) * mm, "end": v(9.2, -6.81) * mm});
            skLineSegment(sketch, "E8.114.14.0", {"start": v(-5.2, -6.01) * mm, "end": v(-5.2, -6.81) * mm});
            skLineSegment(sketch, "E8.117.14.0", {"start": v(-0.4, -6.01) * mm, "end": v(-0.4, -6.81) * mm});
            skLineSegment(sketch, "E8.120.14.0", {"start": v(5.2, -6.01) * mm, "end": v(5.2, -6.81) * mm});
            skLineSegment(sketch, "E8.123.14.0", {"start": v(-4.4, -6.01) * mm, "end": v(-4.4, -6.81) * mm});
            skLineSegment(sketch, "E8.126.14.0", {"start": v(0.4, -6.01) * mm, "end": v(0.4, -6.81) * mm});
            skLineSegment(sketch, "E8.129.14.0", {"start": v(4.4, -6.81) * mm, "end": v(5.2, -6.81) * mm});
            skLineSegment(sketch, "E8.132.14.0", {"start": v(-5.2, -6.81) * mm, "end": v(-4.4, -6.81) * mm});
            skLineSegment(sketch, "E8.135.14.0", {"start": v(-0.4, -6.81) * mm, "end": v(0.4, -6.81) * mm});
            skLineSegment(sketch, "E8.138.14.0", {"start": v(4.4, -6.01) * mm, "end": v(5.2, -6.01) * mm});
            skLineSegment(sketch, "E8.141.14.0", {"start": v(-0.4, -6.01) * mm, "end": v(0.4, -6.01) * mm});
            skLineSegment(sketch, "E8.144.14.0", {"start": v(3.2, -6.01) * mm, "end": v(3.2, -6.81) * mm});
            skLineSegment(sketch, "E8.147.14.0", {"start": v(8, -6.01) * mm, "end": v(8, -6.81) * mm});
            skLineSegment(sketch, "E8.150.14.0", {"start": v(-6.4, -6.01) * mm, "end": v(-6.4, -6.81) * mm});
            skLineSegment(sketch, "E8.153.14.0", {"start": v(-1.6, -6.01) * mm, "end": v(-1.6, -6.81) * mm});
            skLineSegment(sketch, "E8.156.14.0", {"start": v(-5.6, -6.01) * mm, "end": v(-5.6, -6.81) * mm});
            skLineSegment(sketch, "E8.159.14.0", {"start": v(-0.8, -6.01) * mm, "end": v(-0.8, -6.81) * mm});
            skLineSegment(sketch, "E8.162.14.0", {"start": v(4, -6.01) * mm, "end": v(4, -6.81) * mm});
            skLineSegment(sketch, "E8.165.14.0", {"start": v(8.8, -6.01) * mm, "end": v(8.8, -6.81) * mm});
            skLineSegment(sketch, "E8.168.14.0", {"start": v(3.2, -6.81) * mm, "end": v(4, -6.81) * mm});
            skLineSegment(sketch, "E8.171.14.0", {"start": v(8, -6.81) * mm, "end": v(8.8, -6.81) * mm});
            skLineSegment(sketch, "E8.174.14.0", {"start": v(-6.4, -6.81) * mm, "end": v(-5.6, -6.81) * mm});
            skLineSegment(sketch, "E8.177.14.0", {"start": v(-1.6, -6.81) * mm, "end": v(-0.8, -6.81) * mm});
            skLineSegment(sketch, "E8.180.14.0", {"start": v(3.2, -6.01) * mm, "end": v(4, -6.01) * mm});
            skLineSegment(sketch, "E8.183.14.0", {"start": v(8, -6.01) * mm, "end": v(8.8, -6.01) * mm});
            skLineSegment(sketch, "E8.186.14.0", {"start": v(-8.8, -6.01) * mm, "end": v(-8, -6.01) * mm});
            skLineSegment(sketch, "E8.189.14.0", {"start": v(-10, -6.01) * mm, "end": v(-10, -6.81) * mm});
            skLineSegment(sketch, "E8.192.14.0", {"start": v(-10, -6.81) * mm, "end": v(-9.2, -6.81) * mm});
            skLineSegment(sketch, "E8.195.14.0", {"start": v(-10, -6.01) * mm, "end": v(-9.2, -6.01) * mm});
            skLineSegment(sketch, "E8.198.14.0", {"start": v(-2.8, -6.01) * mm, "end": v(-2, -6.01) * mm});
            skLineSegment(sketch, "E8.201.14.0", {"start": v(-4, -6.01) * mm, "end": v(-3.2, -6.01) * mm});
            skLineSegment(sketch, "E8.204.14.0", {"start": v(-5.2, -6.01) * mm, "end": v(-4.4, -6.01) * mm});
            skLineSegment(sketch, "E8.207.14.0", {"start": v(-1.6, -6.01) * mm, "end": v(-0.8, -6.01) * mm});
            skLineSegment(sketch, "E8.0.15.0", {"start": v(6.8, -7.21) * mm, "end": v(6.8, -8.01) * mm});
            skLineSegment(sketch, "E8.3.15.0", {"start": v(6.8, -8.01) * mm, "end": v(7.6, -8.01) * mm});
            skLineSegment(sketch, "E8.6.15.0", {"start": v(6.8, -7.21) * mm, "end": v(7.6, -7.21) * mm});
            skLineSegment(sketch, "E8.9.15.0", {"start": v(6.4, -7.21) * mm, "end": v(6.4, -8.01) * mm});
            skLineSegment(sketch, "E8.12.15.0", {"start": v(5.6, -8.01) * mm, "end": v(6.4, -8.01) * mm});
            skLineSegment(sketch, "E8.15.15.0", {"start": v(5.6, -7.21) * mm, "end": v(6.4, -7.21) * mm});
            skLineSegment(sketch, "E8.18.15.0", {"start": v(10, -7.21) * mm, "end": v(10, -8.01) * mm});
            skLineSegment(sketch, "E8.21.15.0", {"start": v(9.2, -8.01) * mm, "end": v(10, -8.01) * mm});
            skLineSegment(sketch, "E8.24.15.0", {"start": v(9.2, -7.21) * mm, "end": v(10, -7.21) * mm});
            skLineSegment(sketch, "E8.27.15.0", {"start": v(2, -7.21) * mm, "end": v(2, -8.01) * mm});
            skLineSegment(sketch, "E8.30.15.0", {"start": v(-2.8, -7.21) * mm, "end": v(-2.8, -8.01) * mm});
            skLineSegment(sketch, "E8.33.15.0", {"start": v(-7.6, -8.01) * mm, "end": v(-6.8, -8.01) * mm});
            skLineSegment(sketch, "E8.36.15.0", {"start": v(-7.6, -7.21) * mm, "end": v(-6.8, -7.21) * mm});
            skLineSegment(sketch, "E8.39.15.0", {"start": v(-2.8, -8.01) * mm, "end": v(-2, -8.01) * mm});
            skLineSegment(sketch, "E8.42.15.0", {"start": v(2, -8.01) * mm, "end": v(2.8, -8.01) * mm});
            skLineSegment(sketch, "E8.45.15.0", {"start": v(-8.8, -7.21) * mm, "end": v(-8.8, -8.01) * mm});
            skLineSegment(sketch, "E8.48.15.0", {"start": v(-8, -7.21) * mm, "end": v(-8, -8.01) * mm});
            skLineSegment(sketch, "E8.51.15.0", {"start": v(-8.8, -8.01) * mm, "end": v(-8, -8.01) * mm});
            skLineSegment(sketch, "E8.54.15.0", {"start": v(-10, -7.21) * mm, "end": v(0, -7.21) * mm, "construction": true});
            skLineSegment(sketch, "E8.57.15.0", {"start": v(-9.2, -7.21) * mm, "end": v(-9.2, -8.01) * mm});
            skLineSegment(sketch, "E8.60.15.0", {"start": v(-6.4, -7.21) * mm, "end": v(-5.6, -7.21) * mm});
            skLineSegment(sketch, "E8.63.15.0", {"start": v(-7.6, -7.21) * mm, "end": v(-7.6, -8.01) * mm});
            skLineSegment(sketch, "E8.66.15.0", {"start": v(-6.8, -7.21) * mm, "end": v(-6.8, -8.01) * mm});
            skLineSegment(sketch, "E8.69.15.0", {"start": v(2.8, -7.21) * mm, "end": v(2.8, -8.01) * mm});
            skLineSegment(sketch, "E8.72.15.0", {"start": v(7.6, -7.21) * mm, "end": v(7.6, -8.01) * mm});
            skLineSegment(sketch, "E8.75.15.0", {"start": v(-2, -7.21) * mm, "end": v(-2, -8.01) * mm});
            skLineSegment(sketch, "E8.78.15.0", {"start": v(2, -7.21) * mm, "end": v(2.8, -7.21) * mm});
            skLineSegment(sketch, "E8.81.15.0", {"start": v(-4, -7.21) * mm, "end": v(-4, -8.01) * mm});
            skLineSegment(sketch, "E8.84.15.0", {"start": v(0.8, -7.21) * mm, "end": v(0.8, -8.01) * mm});
            skLineSegment(sketch, "E8.87.15.0", {"start": v(5.6, -7.21) * mm, "end": v(5.6, -8.01) * mm});
            skLineSegment(sketch, "E8.90.15.0", {"start": v(-3.2, -7.21) * mm, "end": v(-3.2, -8.01) * mm});
            skLineSegment(sketch, "E8.93.15.0", {"start": v(1.6, -7.21) * mm, "end": v(1.6, -8.01) * mm});
            skLineSegment(sketch, "E8.96.15.0", {"start": v(-4, -8.01) * mm, "end": v(-3.2, -8.01) * mm});
            skLineSegment(sketch, "E8.99.15.0", {"start": v(0.8, -8.01) * mm, "end": v(1.6, -8.01) * mm});
            skLineSegment(sketch, "E8.102.15.0", {"start": v(0.8, -7.21) * mm, "end": v(1.6, -7.21) * mm});
            skLineSegment(sketch, "E8.105.15.0", {"start": v(-10, -8.01) * mm, "end": v(-8.8, -8.01) * mm, "construction": true});
            skLineSegment(sketch, "E8.108.15.0", {"start": v(4.4, -7.21) * mm, "end": v(4.4, -8.01) * mm});
            skLineSegment(sketch, "E8.111.15.0", {"start": v(9.2, -7.21) * mm, "end": v(9.2, -8.01) * mm});
            skLineSegment(sketch, "E8.114.15.0", {"start": v(-5.2, -7.21) * mm, "end": v(-5.2, -8.01) * mm});
            skLineSegment(sketch, "E8.117.15.0", {"start": v(-0.4, -7.21) * mm, "end": v(-0.4, -8.01) * mm});
            skLineSegment(sketch, "E8.120.15.0", {"start": v(5.2, -7.21) * mm, "end": v(5.2, -8.01) * mm});
            skLineSegment(sketch, "E8.123.15.0", {"start": v(-4.4, -7.21) * mm, "end": v(-4.4, -8.01) * mm});
            skLineSegment(sketch, "E8.126.15.0", {"start": v(0.4, -7.21) * mm, "end": v(0.4, -8.01) * mm});
            skLineSegment(sketch, "E8.129.15.0", {"start": v(4.4, -8.01) * mm, "end": v(5.2, -8.01) * mm});
            skLineSegment(sketch, "E8.132.15.0", {"start": v(-5.2, -8.01) * mm, "end": v(-4.4, -8.01) * mm});
            skLineSegment(sketch, "E8.135.15.0", {"start": v(-0.4, -8.01) * mm, "end": v(0.4, -8.01) * mm});
            skLineSegment(sketch, "E8.138.15.0", {"start": v(4.4, -7.21) * mm, "end": v(5.2, -7.21) * mm});
            skLineSegment(sketch, "E8.141.15.0", {"start": v(-0.4, -7.21) * mm, "end": v(0.4, -7.21) * mm});
            skLineSegment(sketch, "E8.144.15.0", {"start": v(3.2, -7.21) * mm, "end": v(3.2, -8.01) * mm});
            skLineSegment(sketch, "E8.147.15.0", {"start": v(8, -7.21) * mm, "end": v(8, -8.01) * mm});
            skLineSegment(sketch, "E8.150.15.0", {"start": v(-6.4, -7.21) * mm, "end": v(-6.4, -8.01) * mm});
            skLineSegment(sketch, "E8.153.15.0", {"start": v(-1.6, -7.21) * mm, "end": v(-1.6, -8.01) * mm});
            skLineSegment(sketch, "E8.156.15.0", {"start": v(-5.6, -7.21) * mm, "end": v(-5.6, -8.01) * mm});
            skLineSegment(sketch, "E8.159.15.0", {"start": v(-0.8, -7.21) * mm, "end": v(-0.8, -8.01) * mm});
            skLineSegment(sketch, "E8.162.15.0", {"start": v(4, -7.21) * mm, "end": v(4, -8.01) * mm});
            skLineSegment(sketch, "E8.165.15.0", {"start": v(8.8, -7.21) * mm, "end": v(8.8, -8.01) * mm});
            skLineSegment(sketch, "E8.168.15.0", {"start": v(3.2, -8.01) * mm, "end": v(4, -8.01) * mm});
            skLineSegment(sketch, "E8.171.15.0", {"start": v(8, -8.01) * mm, "end": v(8.8, -8.01) * mm});
            skLineSegment(sketch, "E8.174.15.0", {"start": v(-6.4, -8.01) * mm, "end": v(-5.6, -8.01) * mm});
            skLineSegment(sketch, "E8.177.15.0", {"start": v(-1.6, -8.01) * mm, "end": v(-0.8, -8.01) * mm});
            skLineSegment(sketch, "E8.180.15.0", {"start": v(3.2, -7.21) * mm, "end": v(4, -7.21) * mm});
            skLineSegment(sketch, "E8.183.15.0", {"start": v(8, -7.21) * mm, "end": v(8.8, -7.21) * mm});
            skLineSegment(sketch, "E8.186.15.0", {"start": v(-8.8, -7.21) * mm, "end": v(-8, -7.21) * mm});
            skLineSegment(sketch, "E8.189.15.0", {"start": v(-10, -7.21) * mm, "end": v(-10, -8.01) * mm});
            skLineSegment(sketch, "E8.192.15.0", {"start": v(-10, -8.01) * mm, "end": v(-9.2, -8.01) * mm});
            skLineSegment(sketch, "E8.195.15.0", {"start": v(-10, -7.21) * mm, "end": v(-9.2, -7.21) * mm});
            skLineSegment(sketch, "E8.198.15.0", {"start": v(-2.8, -7.21) * mm, "end": v(-2, -7.21) * mm});
            skLineSegment(sketch, "E8.201.15.0", {"start": v(-4, -7.21) * mm, "end": v(-3.2, -7.21) * mm});
            skLineSegment(sketch, "E8.204.15.0", {"start": v(-5.2, -7.21) * mm, "end": v(-4.4, -7.21) * mm});
            skLineSegment(sketch, "E8.207.15.0", {"start": v(-1.6, -7.21) * mm, "end": v(-0.8, -7.21) * mm});
            skLineSegment(sketch, "E8.0.16.0", {"start": v(6.8, -8.41) * mm, "end": v(6.8, -9.21) * mm});
            skLineSegment(sketch, "E8.3.16.0", {"start": v(6.8, -9.21) * mm, "end": v(7.6, -9.21) * mm});
            skLineSegment(sketch, "E8.6.16.0", {"start": v(6.8, -8.41) * mm, "end": v(7.6, -8.41) * mm});
            skLineSegment(sketch, "E8.9.16.0", {"start": v(6.4, -8.41) * mm, "end": v(6.4, -9.21) * mm});
            skLineSegment(sketch, "E8.12.16.0", {"start": v(5.6, -9.21) * mm, "end": v(6.4, -9.21) * mm});
            skLineSegment(sketch, "E8.15.16.0", {"start": v(5.6, -8.41) * mm, "end": v(6.4, -8.41) * mm});
            skLineSegment(sketch, "E8.18.16.0", {"start": v(10, -8.41) * mm, "end": v(10, -9.21) * mm});
            skLineSegment(sketch, "E8.21.16.0", {"start": v(9.2, -9.21) * mm, "end": v(10, -9.21) * mm});
            skLineSegment(sketch, "E8.24.16.0", {"start": v(9.2, -8.41) * mm, "end": v(10, -8.41) * mm});
            skLineSegment(sketch, "E8.27.16.0", {"start": v(2, -8.41) * mm, "end": v(2, -9.21) * mm});
            skLineSegment(sketch, "E8.30.16.0", {"start": v(-2.8, -8.41) * mm, "end": v(-2.8, -9.21) * mm});
            skLineSegment(sketch, "E8.33.16.0", {"start": v(-7.6, -9.21) * mm, "end": v(-6.8, -9.21) * mm});
            skLineSegment(sketch, "E8.36.16.0", {"start": v(-7.6, -8.41) * mm, "end": v(-6.8, -8.41) * mm});
            skLineSegment(sketch, "E8.39.16.0", {"start": v(-2.8, -9.21) * mm, "end": v(-2, -9.21) * mm});
            skLineSegment(sketch, "E8.42.16.0", {"start": v(2, -9.21) * mm, "end": v(2.8, -9.21) * mm});
            skLineSegment(sketch, "E8.45.16.0", {"start": v(-8.8, -8.41) * mm, "end": v(-8.8, -9.21) * mm});
            skLineSegment(sketch, "E8.48.16.0", {"start": v(-8, -8.41) * mm, "end": v(-8, -9.21) * mm});
            skLineSegment(sketch, "E8.51.16.0", {"start": v(-8.8, -9.21) * mm, "end": v(-8, -9.21) * mm});
            skLineSegment(sketch, "E8.54.16.0", {"start": v(-10, -8.41) * mm, "end": v(0, -8.41) * mm, "construction": true});
            skLineSegment(sketch, "E8.57.16.0", {"start": v(-9.2, -8.41) * mm, "end": v(-9.2, -9.21) * mm});
            skLineSegment(sketch, "E8.60.16.0", {"start": v(-6.4, -8.41) * mm, "end": v(-5.6, -8.41) * mm});
            skLineSegment(sketch, "E8.63.16.0", {"start": v(-7.6, -8.41) * mm, "end": v(-7.6, -9.21) * mm});
            skLineSegment(sketch, "E8.66.16.0", {"start": v(-6.8, -8.41) * mm, "end": v(-6.8, -9.21) * mm});
            skLineSegment(sketch, "E8.69.16.0", {"start": v(2.8, -8.41) * mm, "end": v(2.8, -9.21) * mm});
            skLineSegment(sketch, "E8.72.16.0", {"start": v(7.6, -8.41) * mm, "end": v(7.6, -9.21) * mm});
            skLineSegment(sketch, "E8.75.16.0", {"start": v(-2, -8.41) * mm, "end": v(-2, -9.21) * mm});
            skLineSegment(sketch, "E8.78.16.0", {"start": v(2, -8.41) * mm, "end": v(2.8, -8.41) * mm});
            skLineSegment(sketch, "E8.81.16.0", {"start": v(-4, -8.41) * mm, "end": v(-4, -9.21) * mm});
            skLineSegment(sketch, "E8.84.16.0", {"start": v(0.8, -8.41) * mm, "end": v(0.8, -9.21) * mm});
            skLineSegment(sketch, "E8.87.16.0", {"start": v(5.6, -8.41) * mm, "end": v(5.6, -9.21) * mm});
            skLineSegment(sketch, "E8.90.16.0", {"start": v(-3.2, -8.41) * mm, "end": v(-3.2, -9.21) * mm});
            skLineSegment(sketch, "E8.93.16.0", {"start": v(1.6, -8.41) * mm, "end": v(1.6, -9.21) * mm});
            skLineSegment(sketch, "E8.96.16.0", {"start": v(-4, -9.21) * mm, "end": v(-3.2, -9.21) * mm});
            skLineSegment(sketch, "E8.99.16.0", {"start": v(0.8, -9.21) * mm, "end": v(1.6, -9.21) * mm});
            skLineSegment(sketch, "E8.102.16.0", {"start": v(0.8, -8.41) * mm, "end": v(1.6, -8.41) * mm});
            skLineSegment(sketch, "E8.105.16.0", {"start": v(-10, -9.21) * mm, "end": v(-8.8, -9.21) * mm, "construction": true});
            skLineSegment(sketch, "E8.108.16.0", {"start": v(4.4, -8.41) * mm, "end": v(4.4, -9.21) * mm});
            skLineSegment(sketch, "E8.111.16.0", {"start": v(9.2, -8.41) * mm, "end": v(9.2, -9.21) * mm});
            skLineSegment(sketch, "E8.114.16.0", {"start": v(-5.2, -8.41) * mm, "end": v(-5.2, -9.21) * mm});
            skLineSegment(sketch, "E8.117.16.0", {"start": v(-0.4, -8.41) * mm, "end": v(-0.4, -9.21) * mm});
            skLineSegment(sketch, "E8.120.16.0", {"start": v(5.2, -8.41) * mm, "end": v(5.2, -9.21) * mm});
            skLineSegment(sketch, "E8.123.16.0", {"start": v(-4.4, -8.41) * mm, "end": v(-4.4, -9.21) * mm});
            skLineSegment(sketch, "E8.126.16.0", {"start": v(0.4, -8.41) * mm, "end": v(0.4, -9.21) * mm});
            skLineSegment(sketch, "E8.129.16.0", {"start": v(4.4, -9.21) * mm, "end": v(5.2, -9.21) * mm});
            skLineSegment(sketch, "E8.132.16.0", {"start": v(-5.2, -9.21) * mm, "end": v(-4.4, -9.21) * mm});
            skLineSegment(sketch, "E8.135.16.0", {"start": v(-0.4, -9.21) * mm, "end": v(0.4, -9.21) * mm});
            skLineSegment(sketch, "E8.138.16.0", {"start": v(4.4, -8.41) * mm, "end": v(5.2, -8.41) * mm});
            skLineSegment(sketch, "E8.141.16.0", {"start": v(-0.4, -8.41) * mm, "end": v(0.4, -8.41) * mm});
            skLineSegment(sketch, "E8.144.16.0", {"start": v(3.2, -8.41) * mm, "end": v(3.2, -9.21) * mm});
            skLineSegment(sketch, "E8.147.16.0", {"start": v(8, -8.41) * mm, "end": v(8, -9.21) * mm});
            skLineSegment(sketch, "E8.150.16.0", {"start": v(-6.4, -8.41) * mm, "end": v(-6.4, -9.21) * mm});
            skLineSegment(sketch, "E8.153.16.0", {"start": v(-1.6, -8.41) * mm, "end": v(-1.6, -9.21) * mm});
            skLineSegment(sketch, "E8.156.16.0", {"start": v(-5.6, -8.41) * mm, "end": v(-5.6, -9.21) * mm});
            skLineSegment(sketch, "E8.159.16.0", {"start": v(-0.8, -8.41) * mm, "end": v(-0.8, -9.21) * mm});
            skLineSegment(sketch, "E8.162.16.0", {"start": v(4, -8.41) * mm, "end": v(4, -9.21) * mm});
            skLineSegment(sketch, "E8.165.16.0", {"start": v(8.8, -8.41) * mm, "end": v(8.8, -9.21) * mm});
            skLineSegment(sketch, "E8.168.16.0", {"start": v(3.2, -9.21) * mm, "end": v(4, -9.21) * mm});
            skLineSegment(sketch, "E8.171.16.0", {"start": v(8, -9.21) * mm, "end": v(8.8, -9.21) * mm});
            skLineSegment(sketch, "E8.174.16.0", {"start": v(-6.4, -9.21) * mm, "end": v(-5.6, -9.21) * mm});
            skLineSegment(sketch, "E8.177.16.0", {"start": v(-1.6, -9.21) * mm, "end": v(-0.8, -9.21) * mm});
            skLineSegment(sketch, "E8.180.16.0", {"start": v(3.2, -8.41) * mm, "end": v(4, -8.41) * mm});
            skLineSegment(sketch, "E8.183.16.0", {"start": v(8, -8.41) * mm, "end": v(8.8, -8.41) * mm});
            skLineSegment(sketch, "E8.186.16.0", {"start": v(-8.8, -8.41) * mm, "end": v(-8, -8.41) * mm});
            skLineSegment(sketch, "E8.189.16.0", {"start": v(-10, -8.41) * mm, "end": v(-10, -9.21) * mm});
            skLineSegment(sketch, "E8.192.16.0", {"start": v(-10, -9.21) * mm, "end": v(-9.2, -9.21) * mm});
            skLineSegment(sketch, "E8.195.16.0", {"start": v(-10, -8.41) * mm, "end": v(-9.2, -8.41) * mm});
            skLineSegment(sketch, "E8.198.16.0", {"start": v(-2.8, -8.41) * mm, "end": v(-2, -8.41) * mm});
            skLineSegment(sketch, "E8.201.16.0", {"start": v(-4, -8.41) * mm, "end": v(-3.2, -8.41) * mm});
            skLineSegment(sketch, "E8.204.16.0", {"start": v(-5.2, -8.41) * mm, "end": v(-4.4, -8.41) * mm});
            skLineSegment(sketch, "E8.207.16.0", {"start": v(-1.6, -8.41) * mm, "end": v(-0.8, -8.41) * mm});
            skLineSegment(sketch, "E9.0.17.0", {"start": v(6.8, -9.61) * mm, "end": v(6.8, -10.41) * mm});
            skLineSegment(sketch, "E9.3.17.0", {"start": v(6.8, -10.41) * mm, "end": v(7.6, -10.41) * mm});
            skLineSegment(sketch, "E9.6.17.0", {"start": v(6.8, -9.61) * mm, "end": v(7.6, -9.61) * mm});
            skLineSegment(sketch, "E9.9.17.0", {"start": v(6.4, -9.61) * mm, "end": v(6.4, -10.41) * mm});
            skLineSegment(sketch, "E9.12.17.0", {"start": v(5.6, -10.41) * mm, "end": v(6.4, -10.41) * mm});
            skLineSegment(sketch, "E9.15.17.0", {"start": v(5.6, -9.61) * mm, "end": v(6.4, -9.61) * mm});
            skLineSegment(sketch, "E9.18.17.0", {"start": v(10, -9.61) * mm, "end": v(10, -10.41) * mm});
            skLineSegment(sketch, "E9.21.17.0", {"start": v(9.2, -10.41) * mm, "end": v(10, -10.41) * mm});
            skLineSegment(sketch, "E9.24.17.0", {"start": v(9.2, -9.61) * mm, "end": v(10, -9.61) * mm});
            skLineSegment(sketch, "E9.27.17.0", {"start": v(2, -9.61) * mm, "end": v(2, -10.41) * mm});
            skLineSegment(sketch, "E9.30.17.0", {"start": v(-2.8, -9.61) * mm, "end": v(-2.8, -10.41) * mm});
            skLineSegment(sketch, "E9.33.17.0", {"start": v(-7.6, -10.41) * mm, "end": v(-6.8, -10.41) * mm});
            skLineSegment(sketch, "E9.36.17.0", {"start": v(-7.6, -9.61) * mm, "end": v(-6.8, -9.61) * mm});
            skLineSegment(sketch, "E9.39.17.0", {"start": v(-2.8, -10.41) * mm, "end": v(-2, -10.41) * mm});
            skLineSegment(sketch, "E9.42.17.0", {"start": v(2, -10.41) * mm, "end": v(2.8, -10.41) * mm});
            skLineSegment(sketch, "E9.45.17.0", {"start": v(-8.8, -9.61) * mm, "end": v(-8.8, -10.41) * mm});
            skLineSegment(sketch, "E9.48.17.0", {"start": v(-8, -9.61) * mm, "end": v(-8, -10.41) * mm});
            skLineSegment(sketch, "E9.51.17.0", {"start": v(-8.8, -10.41) * mm, "end": v(-8, -10.41) * mm});
            skLineSegment(sketch, "E9.54.17.0", {"start": v(-10, -9.61) * mm, "end": v(0, -9.61) * mm, "construction": true});
            skLineSegment(sketch, "E9.57.17.0", {"start": v(-9.2, -9.61) * mm, "end": v(-9.2, -10.41) * mm});
            skLineSegment(sketch, "E9.60.17.0", {"start": v(-6.4, -9.61) * mm, "end": v(-5.6, -9.61) * mm});
            skLineSegment(sketch, "E9.63.17.0", {"start": v(-7.6, -9.61) * mm, "end": v(-7.6, -10.41) * mm});
            skLineSegment(sketch, "E9.66.17.0", {"start": v(-6.8, -9.61) * mm, "end": v(-6.8, -10.41) * mm});
            skLineSegment(sketch, "E9.69.17.0", {"start": v(2.8, -9.61) * mm, "end": v(2.8, -10.41) * mm});
            skLineSegment(sketch, "E9.72.17.0", {"start": v(7.6, -9.61) * mm, "end": v(7.6, -10.41) * mm});
            skLineSegment(sketch, "E9.75.17.0", {"start": v(-2, -9.61) * mm, "end": v(-2, -10.41) * mm});
            skLineSegment(sketch, "E9.78.17.0", {"start": v(2, -9.61) * mm, "end": v(2.8, -9.61) * mm});
            skLineSegment(sketch, "E9.81.17.0", {"start": v(-4, -9.61) * mm, "end": v(-4, -10.41) * mm});
            skLineSegment(sketch, "E9.84.17.0", {"start": v(0.8, -9.61) * mm, "end": v(0.8, -10.41) * mm});
            skLineSegment(sketch, "E9.87.17.0", {"start": v(5.6, -9.61) * mm, "end": v(5.6, -10.41) * mm});
            skLineSegment(sketch, "E9.90.17.0", {"start": v(-3.2, -9.61) * mm, "end": v(-3.2, -10.41) * mm});
            skLineSegment(sketch, "E9.93.17.0", {"start": v(1.6, -9.61) * mm, "end": v(1.6, -10.41) * mm});
            skLineSegment(sketch, "E9.96.17.0", {"start": v(-4, -10.41) * mm, "end": v(-3.2, -10.41) * mm});
            skLineSegment(sketch, "E9.99.17.0", {"start": v(0.8, -10.41) * mm, "end": v(1.6, -10.41) * mm});
            skLineSegment(sketch, "E9.102.17.0", {"start": v(0.8, -9.61) * mm, "end": v(1.6, -9.61) * mm});
            skLineSegment(sketch, "E9.105.17.0", {"start": v(-10, -10.41) * mm, "end": v(-8.8, -10.41) * mm, "construction": true});
            skLineSegment(sketch, "E9.108.17.0", {"start": v(4.4, -9.61) * mm, "end": v(4.4, -10.41) * mm});
            skLineSegment(sketch, "E9.111.17.0", {"start": v(9.2, -9.61) * mm, "end": v(9.2, -10.41) * mm});
            skLineSegment(sketch, "E9.114.17.0", {"start": v(-5.2, -9.61) * mm, "end": v(-5.2, -10.41) * mm});
            skLineSegment(sketch, "E9.117.17.0", {"start": v(-0.4, -9.61) * mm, "end": v(-0.4, -10.41) * mm});
            skLineSegment(sketch, "E9.120.17.0", {"start": v(5.2, -9.61) * mm, "end": v(5.2, -10.41) * mm});
            skLineSegment(sketch, "E9.123.17.0", {"start": v(-4.4, -9.61) * mm, "end": v(-4.4, -10.41) * mm});
            skLineSegment(sketch, "E9.126.17.0", {"start": v(0.4, -9.61) * mm, "end": v(0.4, -10.41) * mm});
            skLineSegment(sketch, "E9.129.17.0", {"start": v(4.4, -10.41) * mm, "end": v(5.2, -10.41) * mm});
            skLineSegment(sketch, "E9.132.17.0", {"start": v(-5.2, -10.41) * mm, "end": v(-4.4, -10.41) * mm});
            skLineSegment(sketch, "E9.135.17.0", {"start": v(-0.4, -10.41) * mm, "end": v(0.4, -10.41) * mm});
            skLineSegment(sketch, "E9.138.17.0", {"start": v(4.4, -9.61) * mm, "end": v(5.2, -9.61) * mm});
            skLineSegment(sketch, "E9.141.17.0", {"start": v(-0.4, -9.61) * mm, "end": v(0.4, -9.61) * mm});
            skLineSegment(sketch, "E9.144.17.0", {"start": v(3.2, -9.61) * mm, "end": v(3.2, -10.41) * mm});
            skLineSegment(sketch, "E9.147.17.0", {"start": v(8, -9.61) * mm, "end": v(8, -10.41) * mm});
            skLineSegment(sketch, "E9.150.17.0", {"start": v(-6.4, -9.61) * mm, "end": v(-6.4, -10.41) * mm});
            skLineSegment(sketch, "E9.153.17.0", {"start": v(-1.6, -9.61) * mm, "end": v(-1.6, -10.41) * mm});
            skLineSegment(sketch, "E9.156.17.0", {"start": v(-5.6, -9.61) * mm, "end": v(-5.6, -10.41) * mm});
            skLineSegment(sketch, "E9.159.17.0", {"start": v(-0.8, -9.61) * mm, "end": v(-0.8, -10.41) * mm});
            skLineSegment(sketch, "E9.162.17.0", {"start": v(4, -9.61) * mm, "end": v(4, -10.41) * mm});
            skLineSegment(sketch, "E9.165.17.0", {"start": v(8.8, -9.61) * mm, "end": v(8.8, -10.41) * mm});
            skLineSegment(sketch, "E9.168.17.0", {"start": v(3.2, -10.41) * mm, "end": v(4, -10.41) * mm});
            skLineSegment(sketch, "E9.171.17.0", {"start": v(8, -10.41) * mm, "end": v(8.8, -10.41) * mm});
            skLineSegment(sketch, "E9.174.17.0", {"start": v(-6.4, -10.41) * mm, "end": v(-5.6, -10.41) * mm});
            skLineSegment(sketch, "E9.177.17.0", {"start": v(-1.6, -10.41) * mm, "end": v(-0.8, -10.41) * mm});
            skLineSegment(sketch, "E9.180.17.0", {"start": v(3.2, -9.61) * mm, "end": v(4, -9.61) * mm});
            skLineSegment(sketch, "E9.183.17.0", {"start": v(8, -9.61) * mm, "end": v(8.8, -9.61) * mm});
            skLineSegment(sketch, "E9.186.17.0", {"start": v(-8.8, -9.61) * mm, "end": v(-8, -9.61) * mm});
            skLineSegment(sketch, "E9.189.17.0", {"start": v(-10, -9.61) * mm, "end": v(-10, -10.41) * mm});
            skLineSegment(sketch, "E9.192.17.0", {"start": v(-10, -10.41) * mm, "end": v(-9.2, -10.41) * mm});
            skLineSegment(sketch, "E9.195.17.0", {"start": v(-10, -9.61) * mm, "end": v(-9.2, -9.61) * mm});
            skLineSegment(sketch, "E9.198.17.0", {"start": v(-2.8, -9.61) * mm, "end": v(-2, -9.61) * mm});
            skLineSegment(sketch, "E9.201.17.0", {"start": v(-4, -9.61) * mm, "end": v(-3.2, -9.61) * mm});
            skLineSegment(sketch, "E9.204.17.0", {"start": v(-5.2, -9.61) * mm, "end": v(-4.4, -9.61) * mm});
            skLineSegment(sketch, "E9.207.17.0", {"start": v(-1.6, -9.61) * mm, "end": v(-0.8, -9.61) * mm});
            skSolve(sketch);
        }
        {
            var Q0;
            {var subQ53=sQuery(id+"F5.wireOp",EDGE,"E6.8.0.1");Q0=makeQuery(id+"F5.imprint","IMPRINT",FACE,{"disambiguationData":[TD([[makeQuery(id+"F5.imprint","IMPRINT",EDGE,{"derivedFrom":subQ53}),-1.0]])]});}
            extrude(context, id + "F6", {"entities" : qUnion([Q0]), "operationType" : NewBodyOperationType.ADD, "depth" : 0.5 * mm});
        }
    });
